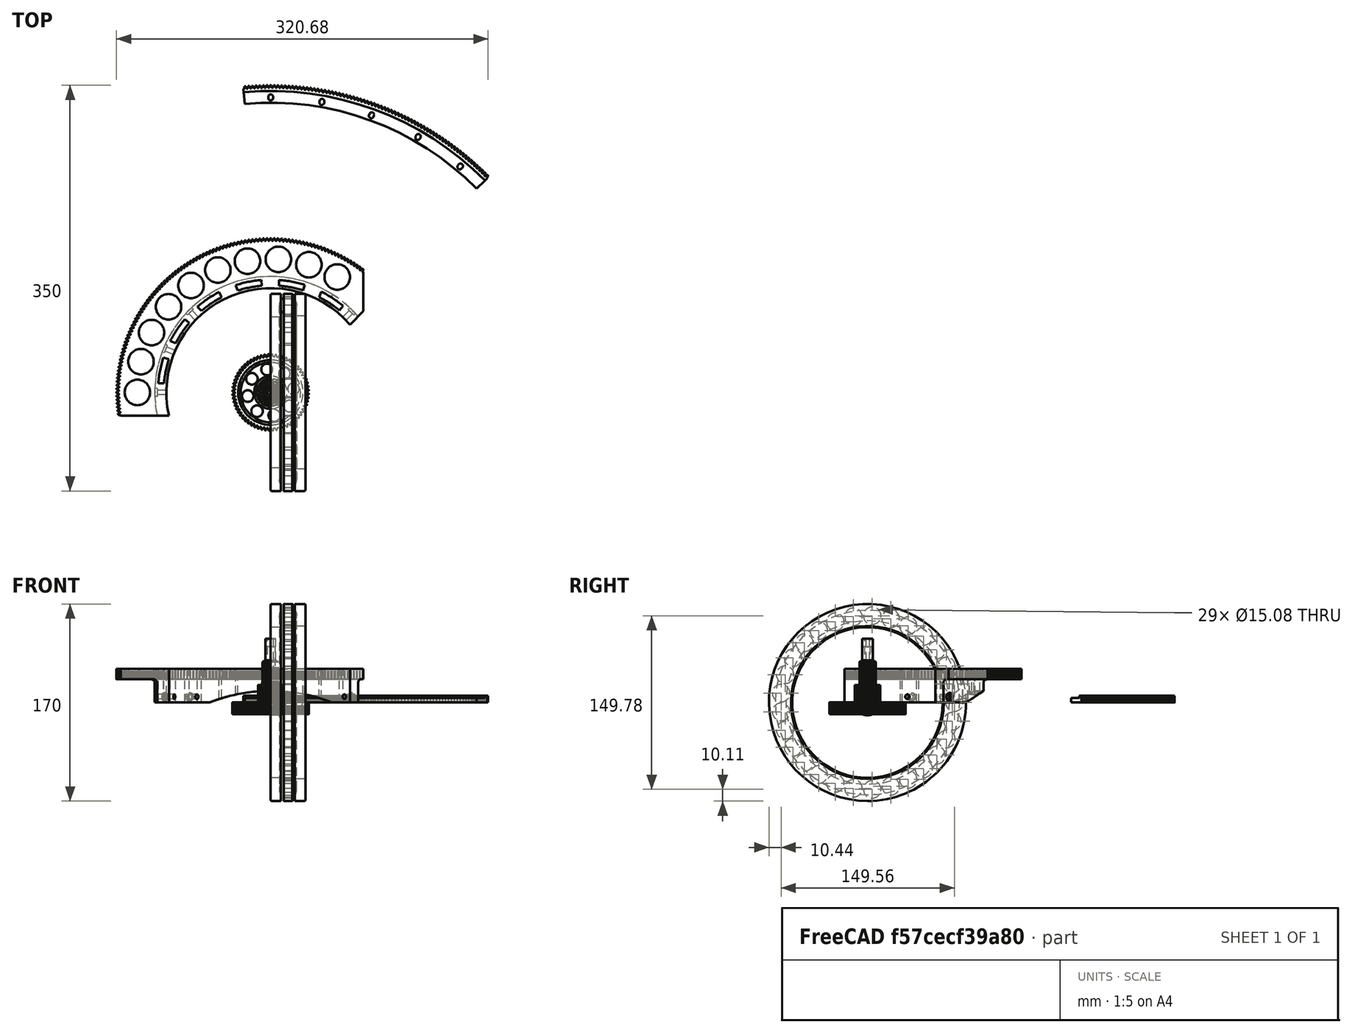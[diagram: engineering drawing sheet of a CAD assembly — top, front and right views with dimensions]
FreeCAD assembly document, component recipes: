
FREECAD ASSEMBLY — COMPONENT RECIPES ("telescope")

This assembly document has 34 components, labeled P0..P33 below (a component is one placed body or linked part). 29 of them carry a construction recipe — the FreeCAD feature program that regenerates the part from scratch, quoted from this document or its linked companion documents; the rest are supplied as boundary geometry only. No exploded tour is included for this assembly.
COMPONENT P0 — recipe-attached ("base-bottom-plate001", modeled in this document).
Construction recipe (the document's own serialized feature program — sketch geometry with constraints, then the solid features built on it; lengths are millimeters unless a unit is written):

FEATURE [Sketcher::SketchObject] Sketch002
  ArcFitTolerance = 0
  AttachmentSupport = -> [XY_Plane]
  ExternalTypes = [0]
  FullyConstrained = true
  MakeInternals = false
  MapMode = 5
  sketch-geometry (1):
    g0: Circle CenterX=0 CenterY=0 CenterZ=0 NormalX=0 NormalY=0 NormalZ=1 AngleXU=0 Radius=7
  constraints (2):
    c: Coincident(g0,g-1)
    c: Diameter(g0) = 14
FEATURE [Sketcher::SketchObject] Sketch
  ArcFitTolerance = 0
  AttachmentSupport = -> [XY_Plane]
  ExternalTypes = [0]
  FullyConstrained = true
  MakeInternals = false
  MapMode = 5
  sketch-geometry (1):
    g0: Circle CenterX=0 CenterY=0 CenterZ=0 NormalX=0 NormalY=0 NormalZ=1 AngleXU=0 Radius=260
  constraints (2):
    c: Coincident(g0,g-1)
    c: Diameter(g0) = 520
FEATURE [PartDesign::Pad] Pad
  AllowMultiFace = false
  Direction = (0,0,1)
  Length = 18
  Length2 = 100
  Profile = -> Sketch
  SideType = 0
  Suppressed = false
  Type = 0
  Type2 = 0
FEATURE [Sketcher::SketchObject] Sketch001
  ArcFitTolerance = 0
  AttachmentSupport = -> [Pad]
  ExternalTypes = [0]
  FullyConstrained = true
  MakeInternals = false
  MapMode = 5
  Placement = pos=(0,0,18) rot=(0,0,1;0rad)
  sketch-geometry (1):
    g0: Circle CenterX=235 CenterY=0 CenterZ=0 NormalX=0 NormalY=0 NormalZ=1 AngleXU=0 Radius=2
  constraints (3):
    c: PointOnObject(g0,g-1)
    c: DistanceX(g0) = 235
    c: Radius(g0) = 2
FEATURE [PartDesign::Pocket] Pocket
  AllowMultiFace = false
  BaseFeature = -> Pad
  Direction = (0,0,-1)
  Length = 5
  Length2 = 100
  Profile = -> Sketch001
  SideType = 0
  Suppressed = false
  Type = 1
  Type2 = 0
FEATURE [PartDesign::PolarPattern] PolarPattern
  Angle = 360
  Axis = -> Sketch001 [N_Axis]
  BaseFeature = -> Pocket
  Mode = 0
  Occurrences = 3
  Offset = 120
  Originals = -> [Pocket]
  SpacingPattern = [0]
  Spacings = [-1,-1]
  Suppressed = false
  TransformMode = 0
FEATURE [PartDesign::Pocket] Pocket001
  BaseFeature = -> PolarPattern
  Direction = (0,0,-1)
  Length = 5
  Length2 = 100
  Profile = -> Sketch002
  Reversed = true
  SideType = 0
  Suppressed = false
  Type = 1
  Type2 = 0
FEATURE [PartDesign::Body] Body  label="base_bottom_plate"
  AllowCompound = true
  Group = -> [Sketch,Pad,Sketch001,Pocket,PolarPattern,Sketch002,Pocket001]
  Origin = -> Origin
  Tip = -> Pocket001
COMPONENT P1 — geometry summary ("bearing-51126_001"; no construction recipe available for this part):
  bounding box: 170.0 x 169.9 x 30.0 mm
  tessellated surface: 256,204 triangles
  volume: 237053 mm^3 (27% of its bounding box)
  symmetry: 2-fold rotationally symmetric about the y axis; revolution-symmetric about the z axis through its bounding-box center; mirror-symmetric across its x mid-plane, z mid-plane
COMPONENT P2 — recipe-attached ("bearing-bottom-location-ring001", modeled in this document).
Construction recipe (the document's own serialized feature program — sketch geometry with constraints, then the solid features built on it; lengths are millimeters unless a unit is written):

FEATURE [Sketcher::SketchObject] Sketch003
  ArcFitTolerance = 0
  AttachmentSupport = -> [XY_Plane003]
  ExternalTypes = [0]
  FullyConstrained = true
  MakeInternals = false
  MapMode = 5
  sketch-geometry (7):
    g0: ArcOfCircle CenterX=0 CenterY=0 CenterZ=0 NormalX=0 NormalY=0 NormalZ=1 AngleXU=0 Radius=60 StartAngle=1.65423 EndAngle=3.58176
    g1: ArcOfCircle CenterX=0 CenterY=0 CenterZ=0 NormalX=0 NormalY=0 NormalZ=1 AngleXU=0 Radius=10 StartAngle=2.0944 EndAngle=3.14159
    g2: LineSegment StartX=-5 StartY=8.66025 StartZ=0 EndX=-5 EndY=59.7913 EndZ=0
    g3: LineSegment [constr] StartX=0 StartY=0 StartZ=0 EndX=-86.6025 EndY=-50 EndZ=0
    g4: LineSegment StartX=-10 StartY=1.2e-15 StartZ=0 EndX=-54.2808 EndY=-25.5655 EndZ=0
    g5: LineSegment [constr] StartX=-10 StartY=1.2e-15 StartZ=0 EndX=0 EndY=0 EndZ=0
    g6: Circle CenterX=0 CenterY=50 CenterZ=0 NormalX=0 NormalY=0 NormalZ=1 AngleXU=0 Radius=2
  constraints (20):
    c: Coincident(g0,g-1)
    c: Coincident(g1,g0)
    c: Vertical(g2)
    c: Coincident(g3,g0)
    c: Angle(g3) = -2.61799
    c: Parallel(g4,g3)
    c: Diameter(g0) = 120
    c: Coincident(g5,g4)
    c: Coincident(g5,g0)
    c: Coincident(g0,g2)
    c: Coincident(g0,g4)
    c: Coincident(g1,g2)
    c: DistanceX(g1) = -5
    c: Diameter(g1) = 20
    c: Distance(g1,g3) = 5
    c: Coincident(g4,g1)
    c: Distance(g3) = 100
    c: PointOnObject(g6,g-2)
    c: Diameter(g6) = 4
    c: DistanceY(g6) = 50
FEATURE [Sketcher::SketchObject] Sketch004
  ArcFitTolerance = 0
  AttachmentSupport = -> [XY_Plane003]
  ExternalTypes = [0]
  FullyConstrained = true
  MakeInternals = false
  MapMode = 5
  sketch-geometry (1):
    g0: Circle CenterX=0 CenterY=0 CenterZ=0 NormalX=0 NormalY=0 NormalZ=1 AngleXU=0 Radius=5.5
  constraints (2):
    c: Coincident(g0,g-1)
    c: Diameter(g0) = 11
FEATURE [Sketcher::SketchObject] Sketch005
  ArcFitTolerance = 0
  AttachmentSupport = -> [XY_Plane003]
  ExternalTypes = [0]
  FullyConstrained = true
  MakeInternals = false
  MapMode = 5
  sketch-geometry (1):
    g0: Circle CenterX=0 CenterY=0 CenterZ=0 NormalX=0 NormalY=0 NormalZ=1 AngleXU=0 Radius=65.25
  constraints (2):
    c: Coincident(g0,g-1)
    c: Diameter(g0) = 130.5
FEATURE [PartDesign::Pad] Pad001
  Direction = (0,0,1)
  Length = 6
  Length2 = 100
  Profile = -> Sketch005
  SideType = 0
  Suppressed = false
  Type = 0
  Type2 = 0
FEATURE [PartDesign::Pocket] Pocket002
  BaseFeature = -> Pad001
  Direction = (0,0,-1)
  Length = 5
  Length2 = 100
  Profile = -> Sketch004
  Reversed = true
  SideType = 0
  Suppressed = false
  Type = 1
  Type2 = 0
FEATURE [PartDesign::Pocket] Pocket003
  BaseFeature = -> Pocket002
  Direction = (0,0,-1)
  Length = 5
  Length2 = 100
  Profile = -> Sketch003
  Reversed = true
  SideType = 0
  Suppressed = false
  Type = 1
  Type2 = 0
FEATURE [PartDesign::PolarPattern] PolarPattern001
  Angle = 360
  Axis = -> Sketch003 [N_Axis]
  BaseFeature = -> Pocket003
  Mode = 0
  Occurrences = 3
  Offset = 120
  Originals = -> [Pocket003]
  SpacingPattern = [0]
  Spacings = [-1,-1]
  Suppressed = false
  TransformMode = 0
FEATURE [PartDesign::Chamfer] Chamfer
  Angle = 45
  Base = -> PolarPattern001 [Edge3,Edge2]
  BaseFeature = -> PolarPattern001
  ChamferType = 0
  FlipDirection = false
  Size = 1
  Size2 = 1
  SupportTransform = true
  Suppressed = false
  UseAllEdges = false
FEATURE [PartDesign::Fillet] Fillet
  Base = -> Chamfer [Edge49,Edge46,Edge54,Edge52,Edge42,Edge40]
  BaseFeature = -> Chamfer
  Radius = 6
  SupportTransform = true
  Suppressed = false
  UseAllEdges = false
FEATURE [Sketcher::SketchObject] Sketch006
  ArcFitTolerance = 0
  AttachmentSupport = -> [Fillet]
  ExternalTypes = [0]
  FullyConstrained = true
  MakeInternals = false
  MapMode = 5
  Placement = pos=(0,0,6) rot=(0,0,1;0rad)
  sketch-geometry (1):
    g0: Circle CenterX=0 CenterY=0 CenterZ=0 NormalX=0 NormalY=0 NormalZ=1 AngleXU=0 Radius=63
  constraints (2):
    c: Coincident(g0,g-1)
    c: Diameter(g0) = 126
FEATURE [PartDesign::Pocket] Pocket004
  BaseFeature = -> Fillet
  Direction = (0,0,-1)
  Length = 3
  Length2 = 100
  Profile = -> Sketch006
  SideType = 0
  Suppressed = false
  Type = 0
  Type2 = 0
FEATURE [PartDesign::Body] Body001  label="bearing-bottom-location-ring"
  AllowCompound = true
  Group = -> [Sketch005,Pad001,Sketch004,Pocket002,Sketch003,Pocket003,PolarPattern001,Chamfer,Fillet,Sketch006,Pocket004]
  Origin = -> Origin003
  Placement = pos=(0,0,18) rot=(0,0,1;0rad)
  Tip = -> Pocket004
COMPONENT P3 — recipe-attached ("m10to14.5-bolt-sleeve001", modeled in this document).
Construction recipe (the document's own serialized feature program — sketch geometry with constraints, then the solid features built on it; lengths are millimeters unless a unit is written):

FEATURE [Sketcher::SketchObject] Sketch007
  ArcFitTolerance = 0
  AttachmentSupport = -> [XY_Plane004]
  ExternalTypes = [0]
  FullyConstrained = true
  MakeInternals = false
  MapMode = 5
  sketch-geometry (2):
    g0: Circle CenterX=0 CenterY=0 CenterZ=0 NormalX=0 NormalY=0 NormalZ=1 AngleXU=0 Radius=5.25
    g1: Circle CenterX=0 CenterY=0 CenterZ=0 NormalX=0 NormalY=0 NormalZ=1 AngleXU=0 Radius=7.25
  constraints (4):
    c: Coincident(g0,g-1)
    c: Coincident(g1,g0)
    c: Diameter(g0) = 10.5
    c: Diameter(g1) = 14.5
FEATURE [PartDesign::Pad] Pad002
  Direction = (0,0,1)
  Length = 17
  Length2 = 100
  Profile = -> Sketch007
  SideType = 0
  Suppressed = false
  Type = 0
  Type2 = 0
FEATURE [PartDesign::Chamfer] Chamfer001
  Angle = 45
  Base = -> Pad002 [Edge3]
  BaseFeature = -> Pad002
  ChamferType = 0
  FlipDirection = false
  Size = 1
  Size2 = 1
  SupportTransform = true
  Suppressed = false
  UseAllEdges = false
FEATURE [PartDesign::Body] Body002  label="m10to14.5-bolt-sleeve"
  AllowCompound = true
  Group = -> [Sketch007,Pad002,Chamfer001]
  Origin = -> Origin004
  Tip = -> Chamfer001
COMPONENT P4 — recipe-attached ("fork-bottom-plate001", modeled in this document).
Construction recipe (the document's own serialized feature program — sketch geometry with constraints, then the solid features built on it; lengths are millimeters unless a unit is written):

FEATURE [Sketcher::SketchObject] Sketch012
  ArcFitTolerance = 0
  AttachmentSupport = -> [XY_Plane009]
  ExternalTypes = [0]
  FullyConstrained = true
  MakeInternals = false
  MapMode = 5
  sketch-geometry (1):
    g0: Circle CenterX=0 CenterY=0 CenterZ=0 NormalX=0 NormalY=0 NormalZ=1 AngleXU=0 Radius=7
  constraints (2):
    c: Coincident(g0,g-1)
    c: Diameter(g0) = 14
FEATURE [Sketcher::SketchObject] Sketch013
  ArcFitTolerance = 0
  AttachmentSupport = -> [XY_Plane009]
  ExternalTypes = [0]
  FullyConstrained = true
  MakeInternals = false
  MapMode = 5
  sketch-geometry (1):
    g0: Circle CenterX=0 CenterY=0 CenterZ=0 NormalX=0 NormalY=0 NormalZ=1 AngleXU=0 Radius=260
  constraints (2):
    c: Coincident(g0,g-1)
    c: Radius(g0) = 260
FEATURE [PartDesign::Pad] Pad003
  AllowMultiFace = false
  Direction = (0,0,1)
  Length = 18
  Length2 = 100
  Profile = -> Sketch013
  SideType = 0
  Suppressed = false
  Type = 0
  Type2 = 0
FEATURE [PartDesign::Pocket] Pocket009
  BaseFeature = -> Pad003
  Direction = (0,0,-1)
  Length = 5
  Length2 = 100
  Profile = -> Sketch012
  Reversed = true
  SideType = 0
  Suppressed = false
  Type = 1
  Type2 = 0
FEATURE [Sketcher::SketchObject] Sketch014
  ArcFitTolerance = 0
  AttachmentSupport = -> [Pocket009]
  ExternalTypes = [0]
  FullyConstrained = true
  MakeInternals = false
  MapMode = 5
  Placement = pos=(0,0,18) rot=(0,0,1;0rad)
  sketch-geometry (4):
    g0: LineSegment StartX=-170 StartY=150 StartZ=0 EndX=170 EndY=150 EndZ=0
    g1: LineSegment StartX=-170 StartY=150 StartZ=0 EndX=-170 EndY=0 EndZ=0
    g2: LineSegment StartX=170 StartY=150 StartZ=0 EndX=170 EndY=0 EndZ=0
    g3: LineSegment StartX=-28 StartY=-227 StartZ=0 EndX=28 EndY=-227 EndZ=0
  constraints (12):
    c: Symmetric(g0,g0,g-2)
    c: DistanceX(g0,g0) = 340
    c: DistanceY(g0) = 150
    c: Coincident(g1,g0)
    c: PointOnObject(g1,g-1)
    c: Vertical(g1)
    c: Coincident(g2,g0)
    c: PointOnObject(g2,g-1)
    c: Vertical(g2)
    c: Symmetric(g3,g3,g-2)
    c: DistanceX(g3,g3) = 56
    c: DistanceY(g3) = -227
FEATURE [PartDesign::Body] Body004  label="fork-bottom-plate"
  AllowCompound = true
  Group = -> [Sketch013,Pad003,Sketch012,Pocket009,Sketch014]
  Origin = -> Origin009
  Placement = pos=(0,0,48) rot=(0,0,1;0.004518rad)
  Tip = -> Pocket009
COMPONENT P5 — recipe-attached ("vertical-axis-main-gear001", modeled in this document).
Construction recipe (the document's own serialized feature program — sketch geometry with constraints, then the solid features built on it; lengths are millimeters unless a unit is written):

FEATURE [PartDesign::FeatureBase] BaseFeature
  BaseFeature = -> InvoluteGear004
  Suppressed = false
FEATURE [Sketcher::SketchObject] Sketch008
  ArcFitTolerance = 0
  AttachmentSupport = -> [BaseFeature]
  ExternalTypes = [0]
  FullyConstrained = true
  MakeInternals = false
  MapMode = 5
  Placement = pos=(0,0,6) rot=(0,0,1;0rad)
  sketch-geometry (1):
    g0: Circle CenterX=0 CenterY=0 CenterZ=0 NormalX=0 NormalY=0 NormalZ=1 AngleXU=0 Radius=260
  constraints (2):
    c: Coincident(g0,g-1)
    c: Diameter(g0) = 520
FEATURE [PartDesign::Pocket] Pocket005
  BaseFeature = -> BaseFeature
  Direction = (0,0,-1)
  Length = 2
  Length2 = 100
  Profile = -> Sketch008
  SideType = 0
  Suppressed = false
  Type = 0
  Type2 = 0
FEATURE [Sketcher::SketchObject] Sketch009
  ArcFitTolerance = 0
  AttachmentSupport = -> [Pocket005]
  ExternalTypes = [0]
  FullyConstrained = true
  MakeInternals = false
  MapMode = 5
  Placement = pos=(0,0,4) rot=(0,0,1;0rad)
  sketch-geometry (1):
    g0: Circle CenterX=0 CenterY=0 CenterZ=0 NormalX=0 NormalY=0 NormalZ=1 AngleXU=0 Radius=250
  constraints (2):
    c: Coincident(g0,g-1)
    c: Diameter(g0) = 500
FEATURE [PartDesign::Pocket] Pocket006
  BaseFeature = -> Pocket005
  Direction = (0,0,-1)
  Length = 5
  Length2 = 100
  Profile = -> Sketch009
  SideType = 0
  Suppressed = false
  Type = 1
  Type2 = 0
FEATURE [Sketcher::SketchObject] Sketch010
  ArcFitTolerance = 0
  AttachmentSupport = -> [Pocket006]
  ExternalTypes = [0]
  FullyConstrained = true
  MakeInternals = false
  MapMode = 5
  Placement = pos=(0,0,4) rot=(0,0,1;0rad)
  sketch-geometry (4):
    g0: ArcOfCircle CenterX=0 CenterY=254 CenterZ=0 NormalX=0 NormalY=0 NormalZ=1 AngleXU=0 Radius=2.1 StartAngle=3.14159 EndAngle=6.28319
    g1: ArcOfCircle CenterX=2e-16 CenterY=255 CenterZ=0 NormalX=0 NormalY=0 NormalZ=1 AngleXU=0 Radius=2.1 StartAngle=4.6e-15 EndAngle=3.14159
    g2: LineSegment StartX=2.1 StartY=254 StartZ=0 EndX=2.1 EndY=255 EndZ=0
    g3: LineSegment StartX=-2.1 StartY=254 StartZ=0 EndX=-2.1 EndY=255 EndZ=0
  constraints (10):
    c: Tangent(g0,g3) = 1.5708
    c: Tangent(g0,g2) = -1.5708
    c: Tangent(g2,g1) = -1.5708
    c: Tangent(g3,g1) = 1.5708
    c: Vertical(g2)
    c: Equal(g0,g1)
    c: PointOnObject(g0,g-2)
    c: Diameter(g0) = 4.2
    c: DistanceY(g2,g2) = 1
    c: DistanceY(g0) = 254
FEATURE [PartDesign::Pocket] Pocket007
  BaseFeature = -> Pocket006
  Direction = (0,0,-1)
  Length = 5
  Length2 = 100
  Profile = -> Sketch010
  SideType = 0
  Suppressed = false
  Type = 1
  Type2 = 0
FEATURE [PartDesign::PolarPattern] PolarPattern002
  Angle = 360
  Axis = -> Sketch010 [N_Axis]
  BaseFeature = -> Pocket007
  Mode = 0
  Occurrences = 36
  Offset = 120
  Originals = -> [Pocket007]
  SpacingPattern = [0]
  Spacings = [-1,-1,-1,-1,-1,-1,-1,-1,-1,-1,-1,-1,-1,-1,-1,-1,-1,-1,-1,-1,-1,-1,-1,-1,-1,-1,-1,-1,-1,-1,-1,-1,-1,-1,-1]
  Suppressed = false
  TransformMode = 0
FEATURE [Sketcher::SketchObject] Sketch011
  ArcFitTolerance = 0
  AttachmentSupport = -> [PolarPattern002]
  ExternalTypes = [0]
  FullyConstrained = true
  MakeInternals = false
  MapMode = 5
  Placement = pos=(0,0,6) rot=(0,0,1;0rad)
  sketch-geometry (3):
    g0: LineSegment StartX=-26.7392 StartY=298.806 StartZ=0 EndX=3.6e-15 EndY=0 EndZ=0
    g1: LineSegment StartX=0 StartY=0 StartZ=0 EndX=213.39 EndY=210.866 EndZ=0
    g2: ArcOfCircle CenterX=0 CenterY=0 CenterZ=0 NormalX=0 NormalY=0 NormalZ=1 AngleXU=0 Radius=300 StartAngle=1.66005 EndAngle=7.06263
  constraints (8):
    c: Coincident(g0,g-1)
    c: Coincident(g1,g0)
    c: Angle(g-2,g0) = 0.0892492
    c: Coincident(g2,g0)
    c: Coincident(g2,g0)
    c: Coincident(g2,g1)
    c: Distance(g0) = 300
    c: Angle(g1,g0) = 0.880597
FEATURE [PartDesign::Pocket] Pocket008
  BaseFeature = -> PolarPattern002
  Direction = (0,0,-1)
  Length = 5
  Length2 = 100
  Profile = -> Sketch011
  SideType = 0
  Suppressed = false
  Type = 1
  Type2 = 0
FEATURE [PartDesign::Body] Body003  label="gear_ring"
  AllowCompound = true
  BaseFeature = -> InvoluteGear004
  Group = -> [BaseFeature,Sketch008,Pocket005,Sketch009,Pocket006,Sketch010,Pocket007,PolarPattern002,Sketch011,Pocket008]
  Origin = -> Origin005
  Tip = -> Pocket008
COMPONENT P6 — same part as P5; its construction recipe is shown at P5.
COMPONENT P7 — same part as P5; its construction recipe is shown at P5.
COMPONENT P8 — same part as P3; its construction recipe is shown at P3.
COMPONENT P9 — recipe-attached ("vertical-axis-motor-mount001", modeled in this document).
Construction recipe (the document's own serialized feature program — sketch geometry with constraints, then the solid features built on it; lengths are millimeters unless a unit is written):

FEATURE [Sketcher::SketchObject] Sketch021
  ArcFitTolerance = 0
  AttachmentSupport = -> [XY_Plane012]
  ExternalTypes = [0]
  FullyConstrained = true
  MakeInternals = false
  MapMode = 5
  sketch-geometry (4):
    g0: ArcOfCircle CenterX=-28 CenterY=15 CenterZ=0 NormalX=0 NormalY=0 NormalZ=1 AngleXU=0 Radius=2 StartAngle=3.14159 EndAngle=6.28319
    g1: ArcOfCircle CenterX=-28 CenterY=25 CenterZ=0 NormalX=0 NormalY=0 NormalZ=1 AngleXU=0 Radius=2 StartAngle=0 EndAngle=3.14159
    g2: LineSegment StartX=-26 StartY=15 StartZ=0 EndX=-26 EndY=25 EndZ=0
    g3: LineSegment StartX=-30 StartY=15 StartZ=0 EndX=-30 EndY=25 EndZ=0
  constraints (10):
    c: Tangent(g0,g3) = 1.5708
    c: Tangent(g0,g2) = -1.5708
    c: Tangent(g2,g1) = -1.5708
    c: Tangent(g3,g1) = 1.5708
    c: Vertical(g2)
    c: Equal(g0,g1)
    c: Radius(g1) = 2
    c: DistanceY(g0,g1) = 10
    c: DistanceY(g0) = 15
    c: DistanceX(g0,g-1) = 28
FEATURE [PartDesign::LinearPattern] LinearPattern
  Direction = -> Sketch021 [H_Axis]
  Length = 56
  Length2 = 100
  Mode = 0
  Mode2 = 0
  Occurrences = 2
  Occurrences2 = 1
  Offset = 56
  Offset2 = 10
  Reversed2 = false
  SpacingPattern = [0]
  SpacingPattern2 = [0]
  Spacings = [-1]
  Suppressed = false
  TransformMode = 0
FEATURE [PartDesign::LinearPattern] LinearPattern001
  Direction = -> Sketch021 [V_Axis]
  Length = 18
  Length2 = 100
  Mode = 0
  Mode2 = 0
  Occurrences = 2
  Occurrences2 = 1
  Offset = 18
  Offset2 = 10
  Reversed2 = false
  SpacingPattern = [0]
  SpacingPattern2 = [0]
  Spacings = [-1]
  Suppressed = false
  TransformMode = 0
FEATURE [Sketcher::SketchObject] Sketch022
  ArcFitTolerance = 0
  ExternalTypes = [0]
  FullyConstrained = true
  MakeInternals = false
  MapMode = 5
  Placement = pos=(0,0,5) rot=(0,0,1;0rad)
  sketch-geometry (4):
    g0: Circle CenterX=-15.5 CenterY=15.5 CenterZ=0 NormalX=0 NormalY=0 NormalZ=1 AngleXU=0 Radius=2
    g1: Circle CenterX=15.5 CenterY=15.5 CenterZ=0 NormalX=0 NormalY=0 NormalZ=1 AngleXU=0 Radius=2
    g2: Circle CenterX=15.5 CenterY=-15.5 CenterZ=0 NormalX=0 NormalY=0 NormalZ=1 AngleXU=0 Radius=2
    g3: Circle CenterX=-15.5 CenterY=-15.5 CenterZ=0 NormalX=0 NormalY=0 NormalZ=1 AngleXU=0 Radius=2
  constraints (9):
    c: Symmetric(g3,g0,g-1)
    c: Symmetric(g0,g1,g-2)
    c: Symmetric(g2,g1,g-1)
    c: Equal(g3,g2)
    c: Equal(g2,g1)
    c: Equal(g1,g0)
    c: DistanceX(g0,g1) = 31
    c: DistanceY(g2,g1) = 31
    c: Diameter(g1) = 4
FEATURE [Sketcher::SketchObject] Sketch023
  ArcFitTolerance = 0
  AttachmentSupport = -> [XY_Plane012]
  ExternalTypes = [0]
  FullyConstrained = true
  MakeInternals = false
  MapMode = 5
  sketch-geometry (5):
    g0: LineSegment StartX=25 StartY=25 StartZ=0 EndX=-25 EndY=25 EndZ=0
    g1: LineSegment StartX=-25 StartY=-25 StartZ=0 EndX=25 EndY=-25 EndZ=0
    g2: Circle [constr] CenterX=0 CenterY=0 CenterZ=0 NormalX=0 NormalY=0 NormalZ=1 AngleXU=0 Radius=35.3553
    g3: LineSegment StartX=-25 StartY=25 StartZ=0 EndX=-25 EndY=-25 EndZ=0
    g4: LineSegment StartX=25 StartY=25 StartZ=0 EndX=25 EndY=-25 EndZ=0
  constraints (14):
    c: Equal(g0,g1)
    c: PointOnObject(g0,g2)
    c: PointOnObject(g1,g2)
    c: PointOnObject(g1,g2)
    c: PointOnObject(g0,g2)
    c: Coincident(g2,g-1)
    c: Horizontal(g0)
    c: DistanceX(g0,g0) = 50
    c: DistanceY(g1,g0) = 50
    c: Horizontal(g1)
    c: Coincident(g0,g3)
    c: Coincident(g3,g1)
    c: Coincident(g0,g4)
    c: Coincident(g4,g1)
FEATURE [PartDesign::Pad] Pad005
  Direction = (0,0,1)
  Length = 10
  Length2 = 100
  Profile = -> Sketch023
  Refine = true
  SideType = 0
  Suppressed = false
  Type = 0
  Type2 = 0
FEATURE [Sketcher::SketchObject] Sketch024
  ArcFitTolerance = 0
  AttachmentSupport = -> [Pad005]
  ExternalTypes = [0]
  FullyConstrained = true
  MakeInternals = false
  MapMode = 5
  Placement = pos=(0,0,10) rot=(0,0,1;0rad)
  sketch-geometry (5):
    g0: LineSegment StartX=21 StartY=21 StartZ=0 EndX=-21 EndY=21 EndZ=0
    g1: LineSegment StartX=-21 StartY=21 StartZ=0 EndX=-21 EndY=-21 EndZ=0
    g2: LineSegment StartX=-21 StartY=-21 StartZ=0 EndX=21 EndY=-21 EndZ=0
    g3: LineSegment StartX=21 StartY=-21 StartZ=0 EndX=21 EndY=21 EndZ=0
    g4: Circle [constr] CenterX=0 CenterY=0 CenterZ=0 NormalX=0 NormalY=0 NormalZ=1 AngleXU=0 Radius=29.6985
  constraints (14):
    c: Coincident(g0,g1)
    c: Coincident(g1,g2)
    c: Coincident(g2,g3)
    c: Coincident(g3,g0)
    c: Equal(g0,g1)
    c: Equal(g0,g2)
    c: Equal(g0,g3)
    c: PointOnObject(g0,g4)
    c: PointOnObject(g1,g4)
    c: PointOnObject(g2,g4)
    c: PointOnObject(g3,g4)
    c: Coincident(g4,g-1)
    c: DistanceX(g0,g0) = 42
    c: Horizontal(g0)
FEATURE [PartDesign::Pocket] Pocket014
  BaseFeature = -> Pad005
  Direction = (0,0,-1)
  Length = 7
  Length2 = 100
  Profile = -> Sketch024
  Refine = true
  SideType = 0
  Suppressed = false
  Type = 0
  Type2 = 0
FEATURE [Sketcher::SketchObject] Sketch025
  ArcFitTolerance = 0
  AttachmentSupport = -> [Pocket014]
  ExternalTypes = [0]
  FullyConstrained = true
  MakeInternals = false
  MapMode = 5
  Placement = pos=(0,0,3) rot=(0,0,1;0rad)
  sketch-geometry (1):
    g0: Circle CenterX=0 CenterY=0 CenterZ=0 NormalX=0 NormalY=0 NormalZ=1 AngleXU=0 Radius=11
  constraints (2):
    c: Coincident(g0,g-1)
    c: Diameter(g0) = 22
FEATURE [PartDesign::Pocket] Pocket015
  BaseFeature = -> Pocket014
  Direction = (0,0,-1)
  Length = 5
  Length2 = 100
  Profile = -> Sketch025
  Refine = true
  SideType = 0
  Suppressed = false
  Type = 1
  Type2 = 0
FEATURE [PartDesign::Pocket] Pocket016
  BaseFeature = -> Pocket015
  Direction = (0,0,-1)
  Length = 5
  Length2 = 100
  Profile = -> Sketch022
  Refine = true
  SideType = 0
  Suppressed = false
  Type = 0
  Type2 = 0
FEATURE [Sketcher::SketchObject] Sketch026
  ArcFitTolerance = 0
  AttachmentSupport = -> [XY_Plane012]
  ExternalGeometry = -> [Pocket016]
  ExternalTypes = [0]
  FullyConstrained = true
  MakeInternals = false
  MapMode = 5
  sketch-geometry (8):
    g0: LineSegment StartX=-25 StartY=25 StartZ=0 EndX=25 EndY=25 EndZ=0
    g1: LineSegment StartX=35 StartY=-7.67949 StartZ=0 EndX=35 EndY=50 EndZ=0
    g2: LineSegment StartX=35 StartY=50 StartZ=0 EndX=-35 EndY=50 EndZ=0
    g3: LineSegment StartX=-35 StartY=50 StartZ=0 EndX=-35 EndY=-7.67949 EndZ=0
    g4: LineSegment StartX=-35 StartY=-7.67949 StartZ=0 EndX=-25 EndY=-25 EndZ=0
    g5: LineSegment StartX=-25 StartY=-25 StartZ=0 EndX=-25 EndY=25 EndZ=0
    g6: LineSegment StartX=35 StartY=-7.67949 StartZ=0 EndX=25 EndY=-25 EndZ=0
    g7: LineSegment StartX=25 StartY=-25 StartZ=0 EndX=25 EndY=25 EndZ=0
  constraints (19):
    c: Coincident(g-3,g0)
    c: Coincident(g0,g-3)
    c: Vertical(g1)
    c: Coincident(g1,g2)
    c: Coincident(g2,g3)
    c: Symmetric(g2,g1,g-2)
    c: Symmetric(g3,g1,g-2)
    c: DistanceX(g2,g2) = 70
    c: DistanceY(g1) = 50
    c: Coincident(g3,g4)
    c: Coincident(g4,g5)
    c: Coincident(g5,g0)
    c: Vertical(g5)
    c: Coincident(g1,g6)
    c: Coincident(g6,g7)
    c: Coincident(g7,g0)
    c: Symmetric(g6,g4,g-2)
    c: Angle(g1,g6) = 2.61799
    c: DistanceY(g6) = -25
FEATURE [PartDesign::Pad] Pad006
  BaseFeature = -> Pocket016
  Direction = (0,0,1)
  Length = 10
  Length2 = 100
  Profile = -> Sketch026
  Refine = true
  SideType = 0
  Suppressed = false
  Type = 0
  Type2 = 0
FEATURE [PartDesign::Pocket] Pocket017
  BaseFeature = -> Pad006
  Direction = (0,0,-1)
  Length = 5
  Length2 = 100
  Profile = -> Sketch021
  Refine = true
  Reversed = true
  SideType = 0
  Suppressed = false
  Type = 1
  Type2 = 0
FEATURE [PartDesign::MultiTransform] MultiTransform
  BaseFeature = -> Pocket017
  Originals = -> [Pocket017]
  Refine = true
  Suppressed = false
  TransformMode = 0
  Transformations = -> [LinearPattern,LinearPattern001]
FEATURE [PartDesign::Fillet] Fillet002
  Base = -> MultiTransform [Edge5,Edge1,Edge2,Edge58,Edge59,Edge8]
  BaseFeature = -> MultiTransform
  Radius = 5
  SupportTransform = true
  Suppressed = false
  UseAllEdges = false
FEATURE [PartDesign::Body] Body007  label="vertical-axis-motor-mount"
  AllowCompound = true
  Group = -> [Sketch023,Pad005,Sketch024,Pocket014,Sketch025,Pocket015,Sketch022,Pocket016,Sketch026,Pad006,Sketch021,Pocket017,MultiTransform,LinearPattern,LinearPattern001,Fillet002]
  Origin = -> Origin012
  Placement = pos=(0,0,232.808) rot=(0,0,1;0rad)
  Tip = -> Fillet002
COMPONENT P10 — recipe-attached ("nema17_001", modeled in this document).
Construction recipe (the document's own serialized feature program — sketch geometry with constraints, then the solid features built on it; lengths are millimeters unless a unit is written):

FEATURE [Sketcher::SketchObject] Sketch027
  ArcFitTolerance = 0
  AttachmentSupport = -> [XY_Plane013]
  ExternalTypes = [0]
  FullyConstrained = true
  MakeInternals = false
  MapMode = 5
  sketch-geometry (5):
    g0: LineSegment StartX=21.15 StartY=21.15 StartZ=0 EndX=-21.15 EndY=21.15 EndZ=0
    g1: LineSegment StartX=-21.15 StartY=21.15 StartZ=0 EndX=-21.15 EndY=-21.15 EndZ=0
    g2: LineSegment StartX=-21.15 StartY=-21.15 StartZ=0 EndX=21.15 EndY=-21.15 EndZ=0
    g3: LineSegment StartX=21.15 StartY=-21.15 StartZ=0 EndX=21.15 EndY=21.15 EndZ=0
    g4: Circle [constr] CenterX=0 CenterY=0 CenterZ=0 NormalX=0 NormalY=0 NormalZ=1 AngleXU=0 Radius=29.9106
  constraints (14):
    c: Coincident(g0,g1)
    c: Coincident(g1,g2)
    c: Coincident(g2,g3)
    c: Coincident(g3,g0)
    c: Equal(g0,g1)
    c: Equal(g0,g2)
    c: Equal(g0,g3)
    c: PointOnObject(g0,g4)
    c: PointOnObject(g1,g4)
    c: PointOnObject(g2,g4)
    c: PointOnObject(g3,g4)
    c: Coincident(g4,g-1)
    c: Horizontal(g0)
    c: DistanceY(g3,g3) = 42.3
FEATURE [PartDesign::Pad] Pad007
  Direction = (0,0,1)
  Length = 40
  Length2 = 100
  Profile = -> Sketch027
  SideType = 0
  Suppressed = false
  Type = 0
  Type2 = 0
FEATURE [Sketcher::SketchObject] Sketch028
  ArcFitTolerance = 0
  AttachmentSupport = -> [Pad007]
  ExternalTypes = [0]
  FullyConstrained = true
  MakeInternals = false
  MapMode = 5
  Placement = pos=(0,0,40) rot=(0,0,1;0rad)
  sketch-geometry (1):
    g0: Circle CenterX=0 CenterY=0 CenterZ=0 NormalX=0 NormalY=0 NormalZ=1 AngleXU=0 Radius=11
  constraints (2):
    c: Coincident(g0,g-1)
    c: Diameter(g0) = 22
FEATURE [PartDesign::Pad] Pad008
  BaseFeature = -> Pad007
  Direction = (0,0,1)
  Length = 2
  Length2 = 100
  Profile = -> Sketch028
  SideType = 0
  Suppressed = false
  Type = 0
  Type2 = 0
FEATURE [Sketcher::SketchObject] Sketch029
  ArcFitTolerance = 0
  AttachmentSupport = -> [Pad008]
  ExternalTypes = [0]
  FullyConstrained = true
  MakeInternals = false
  MapMode = 5
  Placement = pos=(0,0,40) rot=(0,0,1;0rad)
  sketch-geometry (1):
    g0: Circle CenterX=0 CenterY=0 CenterZ=0 NormalX=0 NormalY=0 NormalZ=1 AngleXU=0 Radius=2.5
  constraints (2):
    c: Coincident(g0,g-1)
    c: Diameter(g0) = 5
FEATURE [PartDesign::Pad] Pad009
  BaseFeature = -> Pad008
  Direction = (0,0,1)
  Length = 24
  Length2 = 100
  Profile = -> Sketch029
  SideType = 0
  Suppressed = false
  Type = 0
  Type2 = 0
FEATURE [PartDesign::Chamfer] Chamfer004
  Angle = 45
  Base = -> Pad009 [Edge18]
  BaseFeature = -> Pad009
  ChamferType = 0
  FlipDirection = false
  Size = 0.5
  Size2 = 1
  SupportTransform = true
  Suppressed = false
  UseAllEdges = false
FEATURE [Sketcher::SketchObject] Sketch030
  ArcFitTolerance = 0
  AttachmentSupport = -> [XZ_Plane013]
  ExternalGeometry = -> [Chamfer004]
  ExternalTypes = [0]
  FullyConstrained = true
  MakeInternals = false
  MapMode = 5
  Placement = pos=(0,0,0) rot=(1,0,0;1.5708rad)
  sketch-geometry (4):
    g0: LineSegment StartX=2 StartY=64 StartZ=0 EndX=2.5 EndY=64 EndZ=0
    g1: LineSegment StartX=2.5 StartY=64 StartZ=0 EndX=2.5 EndY=43 EndZ=0
    g2: LineSegment StartX=2.5 StartY=43 StartZ=0 EndX=2 EndY=43 EndZ=0
    g3: LineSegment StartX=2 StartY=43 StartZ=0 EndX=2 EndY=64 EndZ=0
  constraints (12):
    c: Coincident(g0,g1)
    c: Coincident(g1,g2)
    c: Coincident(g2,g3)
    c: Coincident(g3,g0)
    c: Horizontal(g0)
    c: Horizontal(g2)
    c: Vertical(g1)
    c: Vertical(g3)
    c: PointOnObject(g0,g-3)
    c: PointOnObject(g1,g-4)
    c: DistanceX(g2,g2) = 0.5
    c: DistanceY(g1,g1) = 21
FEATURE [PartDesign::Pocket] Pocket018
  BaseFeature = -> Chamfer004
  Direction = (0,1,-2e-16)
  Length = 20
  Length2 = 100
  Profile = -> Sketch030
  SideType = 2
  Suppressed = false
  Type = 1
  Type2 = 0
FEATURE [Sketcher::SketchObject] Sketch031
  ArcFitTolerance = 0
  AttachmentSupport = -> [Pocket018]
  ExternalTypes = [0]
  FullyConstrained = true
  MakeInternals = false
  MapMode = 5
  Placement = pos=(0,0,40) rot=(0,0,1;0rad)
  sketch-geometry (4):
    g0: Circle CenterX=15.5 CenterY=-15.5 CenterZ=0 NormalX=0 NormalY=0 NormalZ=1 AngleXU=0 Radius=1.25
    g1: Circle CenterX=15.5 CenterY=15.5 CenterZ=0 NormalX=0 NormalY=0 NormalZ=1 AngleXU=0 Radius=1.25
    g2: Circle CenterX=-15.5 CenterY=15.5 CenterZ=0 NormalX=0 NormalY=0 NormalZ=1 AngleXU=0 Radius=1.25
    g3: Circle CenterX=-15.5 CenterY=-15.5 CenterZ=0 NormalX=0 NormalY=0 NormalZ=1 AngleXU=0 Radius=1.25
  constraints (9):
    c: Diameter(g0) = 2.5
    c: Symmetric(g1,g0,g-1)
    c: Symmetric(g1,g2,g-2)
    c: Symmetric(g3,g2,g-1)
    c: Equal(g2,g1)
    c: Equal(g1,g3)
    c: Equal(g3,g0)
    c: DistanceX(g2,g1) = 31
    c: DistanceY(g0,g1) = 31
FEATURE [PartDesign::Hole] Hole
  BaseFeature = -> Pocket018
  BaseProfileType = 6
  CustomThreadClearance = 0
  Depth = 4
  DepthType = 0
  Diameter = 1.4
  DrillForDepth = false
  DrillPoint = 1
  DrillPointAngle = 118
  HoleCutCountersinkAngle = 90
  HoleCutCustomValues = false
  HoleCutDepth = 0
  HoleCutDiameter = 1.6
  HoleCutType = 0
  ModelThread = false
  Profile = -> Sketch031
  Suppressed = false
  Tapered = false
  TaperedAngle = 90
  ThreadClass = 0
  ThreadDepth = 4
  ThreadDepthType = 0
  ThreadDiameter = 1.2
  ThreadDirection = 0
  ThreadFit = 0
  ThreadSize = 2
  ThreadType = 1
  Threaded = false
  UseCustomThreadClearance = false
FEATURE [PartDesign::Chamfer] Chamfer005
  Angle = 45
  Base = -> Hole [Edge29,Edge26,Edge31,Edge27]
  BaseFeature = -> Hole
  ChamferType = 0
  FlipDirection = false
  Size = 5
  Size2 = 1
  SupportTransform = true
  Suppressed = false
  UseAllEdges = false
FEATURE [PartDesign::Body] Body008  label="nema17"
  AllowCompound = true
  Group = -> [Sketch027,Pad007,Sketch028,Pad008,Sketch029,Pad009,Chamfer004,Sketch030,Pocket018,Sketch031,Hole,Chamfer005]
  Origin = -> Origin013
  Tip = -> Chamfer005
COMPONENT P11 — recipe-attached ("vertical-axis-motor-gear001", modeled in this document).
Construction recipe (the document's own serialized feature program — sketch geometry with constraints, then the solid features built on it; lengths are millimeters unless a unit is written):

FEATURE [PartDesign::FeatureBase] BaseFeature001
  BaseFeature = -> InvoluteGear005
  Suppressed = false
FEATURE [Sketcher::SketchObject] Sketch032
  ArcFitTolerance = 0
  AttachmentSupport = -> [BaseFeature001]
  ExternalTypes = [0]
  FullyConstrained = true
  MakeInternals = false
  MapMode = 5
  Placement = pos=(0,0,55) rot=(0,0,1;0rad)
  sketch-geometry (2):
    g0: ArcOfCircle CenterX=0 CenterY=0 CenterZ=0 NormalX=0 NormalY=0 NormalZ=1 AngleXU=0 Radius=2.5 StartAngle=0.643501 EndAngle=5.63968
    g1: LineSegment StartX=2 StartY=1.5 StartZ=0 EndX=2 EndY=-1.5 EndZ=0
  constraints (6):
    c: Coincident(g0,g-1)
    c: Diameter(g0) = 5
    c: Vertical(g1)
    c: Coincident(g0,g1)
    c: Coincident(g0,g1)
    c: DistanceX(g0) = 2
FEATURE [PartDesign::Pocket] Pocket019
  BaseFeature = -> BaseFeature001
  Direction = (0,0,-1)
  Length = 25
  Length2 = 100
  Profile = -> Sketch032
  SideType = 0
  Suppressed = false
  Type = 0
  Type2 = 0
FEATURE [Sketcher::SketchObject] Sketch033
  ArcFitTolerance = 0
  AttachmentSupport = -> [XZ_Plane014]
  ExternalGeometry = -> [Pocket019]
  ExternalTypes = [0]
  FullyConstrained = true
  MakeInternals = false
  MapMode = 5
  Placement = pos=(0,0,0) rot=(1,0,0;1.5708rad)
  sketch-geometry (4):
    g0: LineSegment StartX=4.5 StartY=36.4434 StartZ=0 EndX=4.5 EndY=55 EndZ=0
    g1: LineSegment StartX=4.5 StartY=55 StartZ=0 EndX=7 EndY=55 EndZ=0
    g2: LineSegment StartX=7 StartY=55 StartZ=0 EndX=7 EndY=35 EndZ=0
    g3: LineSegment StartX=7 StartY=35 StartZ=0 EndX=4.5 EndY=36.4434 EndZ=0
  constraints (12):
    c: Vertical(g0)
    c: Coincident(g0,g1)
    c: Coincident(g1,g2)
    c: Vertical(g2)
    c: Coincident(g2,g3)
    c: Coincident(g3,g0)
    c: DistanceX(g0) = 4.5
    c: DistanceX(g2) = 7
    c: DistanceY(g2,g2) = 20
    c: Horizontal(g1)
    c: Horizontal(g1,g-3)
    c: Angle(g2,g3) = 1.0472
FEATURE [PartDesign::Groove] Groove
  Angle = 360
  Angle2 = 60
  Axis = (0,2e-16,1)
  Base = (0,0,0)
  BaseFeature = -> Pocket019
  Profile = -> Sketch033
  ReferenceAxis = -> Sketch033 [V_Axis]
  Suppressed = false
  Type = 0
FEATURE [PartDesign::Body] Body009  label="vertical-axis-gear"
  AllowCompound = true
  BaseFeature = -> InvoluteGear005
  Group = -> [BaseFeature001,Sketch032,Pocket019,Sketch033,Groove]
  Origin = -> Origin014
  Tip = -> Groove
COMPONENT P12 — recipe-attached ("fork-rear-plate001", modeled in this document).
Construction recipe (the document's own serialized feature program — sketch geometry with constraints, then the solid features built on it; lengths are millimeters unless a unit is written):

FEATURE [Sketcher::SketchObject] Sketch034
  ArcFitTolerance = 0
  AttachmentSupport = -> [XZ_Plane016]
  ExternalTypes = [0]
  FullyConstrained = true
  MakeInternals = false
  MapMode = 5
  Placement = pos=(0,0,0) rot=(1,0,0;1.5708rad)
  sketch-geometry (7):
    g0: LineSegment StartX=-170 StartY=0 StartZ=0 EndX=170 EndY=0 EndZ=0
    g1: LineSegment StartX=170 StartY=0 StartZ=0 EndX=170 EndY=380 EndZ=0
    g2: LineSegment StartX=170 StartY=380 StartZ=0 EndX=90 EndY=380 EndZ=0
    g3: LineSegment StartX=-170 StartY=380 StartZ=0 EndX=-170 EndY=0 EndZ=0
    g4: ArcOfCircle CenterX=0 CenterY=500 CenterZ=0 NormalX=0 NormalY=0 NormalZ=1 AngleXU=0 Radius=150 StartAngle=4.06889 EndAngle=5.35589
    g5: LineSegment StartX=-90 StartY=380 StartZ=0 EndX=-170 EndY=380 EndZ=0
    g6: GeomPoint [constr] X=0 Y=350 Z=0
  constraints (19):
    c: Coincident(g0,g1)
    c: Coincident(g1,g2)
    c: Coincident(g5,g3)
    c: Coincident(g3,g0)
    c: Horizontal(g0)
    c: Vertical(g1)
    c: Vertical(g3)
    c: PointOnObject(g0,g-1)
    c: Symmetric(g1,g5,g-2)
    c: DistanceY(g1,g1) = 380
    c: DistanceX(g0,g0) = 340
    c: Tangent(g2,g5)
    c: Coincident(g4,g5)
    c: Coincident(g4,g2)
    c: PointOnObject(g4,g-2)
    c: PointOnObject(g6,g-2)
    c: PointOnObject(g6,g4)
    c: DistanceY(g-1,g6) = 350
    c: DistanceX(g4,g2) = 180
FEATURE [PartDesign::Pad] Pad010
  AllowMultiFace = false
  Direction = (0,-1,-1.035e-13)
  Length = 18
  Length2 = 100
  Placement = pos=(0,0,0) rot=(1,0,0;1.5708rad)
  Profile = -> Sketch034
  SideType = 0
  Suppressed = false
  Type = 0
  Type2 = 0
FEATURE [PartDesign::Body] Body010  label="fork-rear-plate"
  AllowCompound = true
  Group = -> [Sketch034,Pad010]
  Origin = -> Origin016
  Tip = -> Pad010
COMPONENT P13 — recipe-attached ("fork-side-plate001", modeled in this document).
Construction recipe (the document's own serialized feature program — sketch geometry with constraints, then the solid features built on it; lengths are millimeters unless a unit is written):

FEATURE [Sketcher::SketchObject] Sketch035
  ArcFitTolerance = 0
  AttachmentSupport = -> [YZ_Plane017]
  ExternalTypes = [0]
  FullyConstrained = true
  MakeInternals = false
  MapMode = 5
  Placement = pos=(0,0,0) rot=(0.57735,0.57735,0.57735;2.0944rad)
  sketch-geometry (5):
    g0: ArcOfCircle CenterX=0 CenterY=580 CenterZ=0 NormalX=0 NormalY=0 NormalZ=1 AngleXU=0 Radius=95 StartAngle=0.495618 EndAngle=3.41262
    g1: ArcOfCircle CenterX=-765.98 CenterY=367.162 CenterZ=0 NormalX=0 NormalY=0 NormalZ=1 AngleXU=0 Radius=700 StartAngle=5.73104 EndAngle=6.55421
    g2: ArcOfCircle CenterX=-708.138 CenterY=197.162 CenterZ=0 NormalX=0 NormalY=0 NormalZ=1 AngleXU=0 Radius=900 StartAngle=6.06233 EndAngle=6.7788
    g3: LineSegment StartX=-170 StartY=-2.274e-13 StartZ=0 EndX=170 EndY=-1.705e-13 EndZ=0
    g4: Circle CenterX=0 CenterY=580 CenterZ=0 NormalX=0 NormalY=0 NormalZ=1 AngleXU=0 Radius=6
  constraints (16):
    c: PointOnObject(g0,g-2)
    c: Radius(g0) = 95
    c: DistanceY(g-1,g0) = 580
    c: PointOnObject(g1,g-1)
    c: PointOnObject(g2,g-1)
    c: Tangent(g2,g0)
    c: Coincident(g3,g1)
    c: Coincident(g3,g2)
    c: DistanceX(g3,g3) = 340
    c: DistanceX(g1,g-1) = 170
    c: Radius(g1) = 700
    c: Radius(g2) = 900
    c: Coincident(g0,g2)
    c: Tangent(g0,g1) = 1.5708
    c: Coincident(g4,g0)
    c: Radius(g4) = 6
FEATURE [PartDesign::Pad] Pad011
  AllowMultiFace = false
  Direction = (1,-1.128e-13,1.13e-13)
  Length = 18
  Length2 = 100
  Placement = pos=(0,0,0) rot=(0.57735,0.57735,0.57735;2.0944rad)
  Profile = -> Sketch035
  SideType = 2
  Suppressed = false
  Type = 0
  Type2 = 0
FEATURE [Sketcher::SketchObject] Sketch036
  ArcFitTolerance = 0
  AttachmentSupport = -> [Pad011]
  ExternalGeometry = -> [Pad011]
  ExternalTypes = [0]
  FullyConstrained = true
  MakeInternals = false
  MapMode = 5
  Placement = pos=(9,-1.0152e-12,1.0172e-12) rot=(0.57735,0.57735,0.57735;2.0944rad)
  sketch-geometry (5):
    g0: Circle [constr] CenterX=0 CenterY=580 CenterZ=0 NormalX=0 NormalY=0 NormalZ=1 AngleXU=0 Radius=75
    g1: LineSegment [constr] StartX=0 StartY=580 StartZ=0 EndX=-53.033 EndY=526.967 EndZ=0
    g2: LineSegment [constr] StartX=0 StartY=580 StartZ=0 EndX=53.033 EndY=526.967 EndZ=0
    g3: Circle CenterX=-53.033 CenterY=526.967 CenterZ=0 NormalX=0 NormalY=0 NormalZ=1 AngleXU=0 Radius=3
    g4: Circle CenterX=53.033 CenterY=526.967 CenterZ=0 NormalX=0 NormalY=0 NormalZ=1 AngleXU=0 Radius=3
  constraints (12):
    c: Coincident(g0,g-3)
    c: Coincident(g1,g0)
    c: PointOnObject(g1,g0)
    c: Coincident(g2,g0)
    c: PointOnObject(g2,g0)
    c: Angle(g1,g2) = 1.5708
    c: Angle(g1) = -2.35619
    c: Radius(g0) = 75
    c: Coincident(g3,g1)
    c: Coincident(g4,g2)
    c: Equal(g4,g3)
    c: Radius(g4) = 3
FEATURE [PartDesign::Pocket] Pocket020
  AllowMultiFace = false
  BaseFeature = -> Pad011
  Direction = (-1,1.125e-13,-1.129e-13)
  Length = 5
  Length2 = 100
  Placement = pos=(0,0,0) rot=(0.57735,0.57735,0.57735;2.0944rad)
  Profile = -> Sketch036
  SideType = 0
  Suppressed = false
  Type = 1
  Type2 = 0
FEATURE [PartDesign::Line] DatumLine
  AttacherType = Attacher::AttachEngineLine
  AttachmentSupport = -> [Pocket020]
  Length = 18
  MapMode = 19
  Placement = pos=(9,6.45244e-11,580) rot=(0.57735,0.57735,0.57735;2.0944rad)
  ResizeMode = 0
FEATURE [Sketcher::SketchObject] Sketch037
  ArcFitTolerance = 0
  AttachmentSupport = -> [Pocket020]
  ExternalGeometry = -> [Pocket020]
  ExternalTypes = [0]
  FullyConstrained = true
  MakeInternals = false
  MapMode = 5
  Placement = pos=(9,-1.0152e-12,1.0172e-12) rot=(0.57735,0.57735,0.57735;2.0944rad)
  sketch-geometry (1):
    g0: LineSegment StartX=2.416e-13 StartY=580 StartZ=0 EndX=0 EndY=0 EndZ=0
  constraints (2):
    c: Coincident(g0,g-3)
    c: Coincident(g0,g-1)
FEATURE [PartDesign::Body] Body011  label="fork-side-plate"
  AllowCompound = true
  Group = -> [Sketch035,Pad011,Sketch036,Pocket020,DatumLine,Sketch037]
  Origin = -> Origin017
  Tip = -> Pocket020
COMPONENT P14 — same part as P13; its construction recipe is shown at P13.
COMPONENT P15 — recipe-attached ("tube-main001", modeled in this document).
Construction recipe (the document's own serialized feature program — sketch geometry with constraints, then the solid features built on it; lengths are millimeters unless a unit is written):

FEATURE [Sketcher::SketchObject] Sketch059
  ArcFitTolerance = 0
  AttachmentSupport = -> [XY_Plane023]
  ExternalTypes = [0]
  FullyConstrained = true
  MakeInternals = false
  MapMode = 5
  sketch-geometry (2):
    g0: Circle CenterX=0 CenterY=0 CenterZ=0 NormalX=0 NormalY=0 NormalZ=1 AngleXU=0 Radius=140
    g1: Circle CenterX=0 CenterY=0 CenterZ=0 NormalX=0 NormalY=0 NormalZ=1 AngleXU=0 Radius=143
  constraints (4):
    c: Coincident(g0,g-1)
    c: Coincident(g1,g0)
    c: Radius(g1) = 143
    c: Radius(g0) = 140
FEATURE [PartDesign::Pad] Pad020
  AllowMultiFace = false
  Direction = (0,0,1)
  Length = 1120
  Length2 = 100
  Profile = -> Sketch059
  SideType = 0
  Suppressed = false
  Type = 0
  Type2 = 0
FEATURE [PartDesign::Plane] DatumPlane004
  AttachmentOffset = pos=(0,0,-20) rot=(0,0,1;0rad)
  AttachmentSupport = -> [Pad020]
  Length = 404.321
  MapMode = 5
  Placement = pos=(0,0,20) rot=(1,0,0;3.14159rad)
  ResizeMode = 0
  Width = 346.236
FEATURE [Sketcher::SketchObject] Sketch060
  ArcFitTolerance = 0
  AttachmentSupport = -> [DatumPlane004]
  ExternalGeometry = -> [Pad020]
  ExternalTypes = [0]
  FullyConstrained = true
  MakeInternals = false
  MapMode = 5
  Placement = pos=(0,0,20) rot=(1,0,0;3.14159rad)
  sketch-geometry (2):
    g0: Circle CenterX=0 CenterY=0 CenterZ=0 NormalX=0 NormalY=0 NormalZ=1 AngleXU=0 Radius=140
    g1: Circle CenterX=0 CenterY=0 CenterZ=0 NormalX=0 NormalY=0 NormalZ=1 AngleXU=0 Radius=103
  constraints (4):
    c: Coincident(g0,g-1)
    c: Coincident(g1,g0)
    c: Equal(g-3,g0)
    c: Radius(g1) = 103
FEATURE [PartDesign::Pad] Pad021
  AllowMultiFace = false
  BaseFeature = -> Pad020
  Direction = (0,0,-1)
  Length = 10
  Length2 = 100
  Profile = -> Sketch060
  Reversed = true
  SideType = 0
  Suppressed = false
  Type = 0
  Type2 = 0
FEATURE [PartDesign::Plane] DatumPlane005
  AttachmentOffset = pos=(0,0,150) rot=(0,0,1;0rad)
  AttachmentSupport = -> [YZ_Plane023]
  Length = 397.947
  MapMode = 5
  Placement = pos=(150,-1.69198e-11,1.69531e-11) rot=(0.57735,0.57735,0.57735;2.0944rad)
  ResizeMode = 0
  Width = 1259.03
FEATURE [Sketcher::SketchObject] Sketch061
  ArcFitTolerance = 0
  AttachmentSupport = -> [DatumPlane005]
  ExternalTypes = [0]
  FullyConstrained = true
  MakeInternals = false
  MapMode = 5
  Placement = pos=(150,-1.69198e-11,1.69531e-11) rot=(0.57735,0.57735,0.57735;2.0944rad)
  sketch-geometry (1):
    g0: Circle CenterX=0 CenterY=420 CenterZ=0 NormalX=0 NormalY=0 NormalZ=1 AngleXU=0 Radius=90
  constraints (3):
    c: PointOnObject(g0,g-2)
    c: DistanceY(g0) = 420
    c: Radius(g0) = 90
FEATURE [PartDesign::Pad] Pad022
  AllowMultiFace = false
  BaseFeature = -> Pad021
  Direction = (1,0,0)
  Length = 23
  Length2 = 100
  Profile = -> Sketch061
  ReferenceAxis = -> Sketch061 [N_Axis]
  Reversed = true
  SideType = 0
  Suppressed = false
  Type = 2
  Type2 = 0
FEATURE [Sketcher::SketchObject] Sketch062
  ArcFitTolerance = 0
  AttachmentSupport = -> [Pad022]
  ExternalTypes = [0]
  FullyConstrained = true
  MakeInternals = false
  MapMode = 5
  Placement = pos=(150,-1.6926e-11,1.6956e-11) rot=(0.57735,0.57735,0.57735;2.0944rad)
  sketch-geometry (1):
    g0: Circle CenterX=0 CenterY=420 CenterZ=0 NormalX=0 NormalY=0 NormalZ=1 AngleXU=0 Radius=65
  constraints (2):
    c: Coincident(g0,g-3)
    c: Radius(g0) = 65
FEATURE [PartDesign::Pad] Pad023
  AllowMultiFace = false
  BaseFeature = -> Pad022
  Direction = (1,-1.127e-13,1.129e-13)
  Length = 20
  Length2 = 100
  Profile = -> Sketch062
  SideType = 0
  Suppressed = false
  Type = 0
  Type2 = 0
FEATURE [Sketcher::SketchObject] Sketch063
  ArcFitTolerance = 0
  AttachmentSupport = -> [Pad023]
  ExternalGeometry = -> [Pad023]
  ExternalTypes = [0]
  FullyConstrained = true
  MakeInternals = false
  MapMode = 5
  Placement = pos=(170,-1.91539e-11,1.91845e-11) rot=(0.57735,0.57735,0.57735;2.0944rad)
  sketch-geometry (2):
    g0: Circle CenterX=0 CenterY=420 CenterZ=0 NormalX=0 NormalY=0 NormalZ=1 AngleXU=0 Radius=32
    g1: Circle CenterX=0 CenterY=420 CenterZ=0 NormalX=0 NormalY=0 NormalZ=1 AngleXU=0 Radius=25
  constraints (4):
    c: Coincident(g0,g-3)
    c: Radius(g0) = 32
    c: Coincident(g1,g0)
    c: Radius(g1) = 25
FEATURE [PartDesign::Pad] Pad024
  AllowMultiFace = false
  BaseFeature = -> Pad023
  Direction = (1,-1.126e-13,1.13e-13)
  Length = 1
  Length2 = 100
  Profile = -> Sketch063
  SideType = 0
  Suppressed = false
  Type = 0
  Type2 = 0
FEATURE [PartDesign::Plane] DatumPlane006
  AttachmentOffset = pos=(0,0,-150) rot=(0,0,1;0rad)
  AttachmentSupport = -> [YZ_Plane023]
  Length = 397.947
  MapMode = 5
  Placement = pos=(-150,1.69198e-11,-1.69531e-11) rot=(0.57735,0.57735,0.57735;2.0944rad)
  ResizeMode = 0
  Width = 1259.03
FEATURE [Sketcher::SketchObject] Sketch064
  ArcFitTolerance = 0
  AttachmentSupport = -> [DatumPlane006]
  ExternalGeometry = -> [Pad024]
  ExternalTypes = [0]
  FullyConstrained = true
  MakeInternals = false
  MapMode = 5
  Placement = pos=(-150,1.69198e-11,-1.69531e-11) rot=(0.57735,0.57735,0.57735;2.0944rad)
  sketch-geometry (1):
    g0: Circle CenterX=0 CenterY=420 CenterZ=0 NormalX=0 NormalY=0 NormalZ=1 AngleXU=0 Radius=90
  constraints (2):
    c: Coincident(g0,g-3)
    c: Equal(g0,g-3)
FEATURE [PartDesign::Pad] Pad025
  AllowMultiFace = false
  BaseFeature = -> Pad024
  Direction = (1,-1.128e-13,1.13e-13)
  Length = 10
  Length2 = 100
  Profile = -> Sketch064
  SideType = 0
  Suppressed = false
  Type = 3
  Type2 = 0
  UpToFace = -> Pad024 [Face1]
FEATURE [Sketcher::SketchObject] Sketch065
  ArcFitTolerance = 0
  AttachmentSupport = -> [Pad025]
  ExternalGeometry = -> [Pad025]
  ExternalTypes = [0]
  FullyConstrained = true
  MakeInternals = false
  MapMode = 5
  Placement = pos=(-150,1.6926e-11,-1.6956e-11) rot=(-0.57735,0.57735,0.57735;4.18879rad)
  sketch-geometry (1):
    g0: Circle CenterX=0 CenterY=420 CenterZ=0 NormalX=0 NormalY=0 NormalZ=1 AngleXU=0 Radius=65
  constraints (2):
    c: Coincident(g0,g-3)
    c: Equal(g-4,g0)
FEATURE [PartDesign::Pad] Pad026
  AllowMultiFace = false
  BaseFeature = -> Pad025
  Direction = (-1,1.127e-13,-1.129e-13)
  Length = 20
  Length2 = 100
  Profile = -> Sketch065
  SideType = 0
  Suppressed = false
  Type = 0
  Type2 = 0
FEATURE [Sketcher::SketchObject] Sketch066
  ArcFitTolerance = 0
  AttachmentSupport = -> [Pad026]
  ExternalGeometry = -> [Pad026]
  ExternalTypes = [0]
  FullyConstrained = true
  MakeInternals = false
  MapMode = 5
  Placement = pos=(-170,1.91539e-11,-1.91845e-11) rot=(-0.57735,0.57735,0.57735;4.18879rad)
  sketch-geometry (2):
    g0: Circle CenterX=0 CenterY=420 CenterZ=0 NormalX=0 NormalY=0 NormalZ=1 AngleXU=0 Radius=25
    g1: Circle CenterX=0 CenterY=420 CenterZ=0 NormalX=0 NormalY=0 NormalZ=1 AngleXU=0 Radius=32
  constraints (4):
    c: Coincident(g0,g-4)
    c: Coincident(g1,g0)
    c: Equal(g1,g-3)
    c: Equal(g0,g-4)
FEATURE [PartDesign::Pad] Pad027
  AllowMultiFace = false
  BaseFeature = -> Pad026
  Direction = (-1,1.126e-13,-1.13e-13)
  Length = 1
  Length2 = 100
  Profile = -> Sketch066
  SideType = 0
  Suppressed = false
  Type = 0
  Type2 = 0
FEATURE [Sketcher::SketchObject] Sketch067
  ArcFitTolerance = 0
  AttachmentSupport = -> [Pad027]
  ExternalGeometry = -> [Pad027]
  ExternalTypes = [0]
  FullyConstrained = true
  MakeInternals = false
  MapMode = 5
  Placement = pos=(170,-1.91539e-11,1.91845e-11) rot=(0.57735,0.57735,0.57735;2.0944rad)
  sketch-geometry (1):
    g0: Circle CenterX=0 CenterY=420 CenterZ=0 NormalX=0 NormalY=0 NormalZ=1 AngleXU=0 Radius=5.25
  constraints (2):
    c: Coincident(g0,g-3)
    c: Radius(g0) = 5.25
FEATURE [PartDesign::Pocket] Pocket033
  AllowMultiFace = false
  BaseFeature = -> Pad027
  Direction = (-1,1.126e-13,-1.13e-13)
  Length = 7
  Length2 = 100
  Profile = -> Sketch067
  SideType = 0
  Suppressed = false
  Type = 0
  Type2 = 0
FEATURE [Sketcher::SketchObject] Sketch068
  ArcFitTolerance = 0
  AttachmentSupport = -> [Pocket033]
  ExternalGeometry = -> [Pocket033]
  ExternalTypes = [0]
  FullyConstrained = true
  MakeInternals = false
  MapMode = 5
  Placement = pos=(163,-1.85315e-11,1.8851e-11) rot=(0.57735,0.57735,0.57735;2.0944rad)
  sketch-geometry (1):
    g0: Circle CenterX=0 CenterY=420 CenterZ=0 NormalX=0 NormalY=0 NormalZ=1 AngleXU=0 Radius=4.25
  constraints (2):
    c: Coincident(g0,g-3)
    c: Radius(g0) = 4.25
FEATURE [PartDesign::Pocket] Pocket034
  AllowMultiFace = false
  BaseFeature = -> Pocket033
  Direction = (-1,1.136e-13,-1.156e-13)
  Length = 15
  Length2 = 100
  Profile = -> Sketch068
  SideType = 0
  Suppressed = false
  Type = 0
  Type2 = 0
FEATURE [Sketcher::SketchObject] Sketch069
  ArcFitTolerance = 0
  AttachmentSupport = -> [Pocket034]
  ExternalGeometry = -> [Pocket034]
  ExternalTypes = [0]
  FullyConstrained = true
  MakeInternals = false
  MapMode = 5
  Placement = pos=(-170,1.91539e-11,-1.91845e-11) rot=(-0.57735,0.57735,0.57735;4.18879rad)
  sketch-geometry (1):
    g0: Circle CenterX=0 CenterY=420 CenterZ=0 NormalX=0 NormalY=0 NormalZ=1 AngleXU=0 Radius=5.25
  constraints (2):
    c: Coincident(g0,g-3)
    c: Radius(g0) = 5.25
FEATURE [PartDesign::Pocket] Pocket035
  AllowMultiFace = false
  BaseFeature = -> Pocket034
  Direction = (1,-1.126e-13,1.13e-13)
  Length = 7
  Length2 = 100
  Profile = -> Sketch069
  SideType = 0
  Suppressed = false
  Type = 0
  Type2 = 0
FEATURE [Sketcher::SketchObject] Sketch070
  ArcFitTolerance = 0
  AttachmentSupport = -> [Pocket035]
  ExternalGeometry = -> [Pocket035]
  ExternalTypes = [0]
  FullyConstrained = true
  MakeInternals = false
  MapMode = 5
  Placement = pos=(-163,1.82364e-11,-1.83408e-11) rot=(-0.57735,0.57735,0.57735;4.18879rad)
  sketch-geometry (1):
    g0: Circle CenterX=0 CenterY=420 CenterZ=0 NormalX=0 NormalY=0 NormalZ=1 AngleXU=0 Radius=4.25
  constraints (2):
    c: Coincident(g0,g-3)
    c: Radius(g0) = 4.25
FEATURE [PartDesign::Pocket] Pocket036
  AllowMultiFace = false
  BaseFeature = -> Pocket035
  Direction = (1,-1.118e-13,1.125e-13)
  Length = 15
  Length2 = 100
  Profile = -> Sketch070
  SideType = 0
  Suppressed = false
  Type = 0
  Type2 = 0
FEATURE [PartDesign::Body] Body014  label="tube-main"
  AllowCompound = true
  Group = -> [Sketch059,Pad020,DatumPlane004,Sketch060,Pad021,DatumPlane005,Sketch061,Pad022,Sketch062,Pad023,Sketch063,Pad024,DatumPlane006,Sketch064,Pad025,Sketch065,Pad026,Sketch066,Pad027,Sketch067,Pocket033,Sketch068,Pocket034,Sketch069,Pocket035,Sketch070,Pocket036]
  Origin = -> Origin023
  Tip = -> Pocket036
COMPONENT P16 — recipe-attached ("tube-main-gear001", modeled in this document).
Construction recipe (the document's own serialized feature program — sketch geometry with constraints, then the solid features built on it; lengths are millimeters unless a unit is written):

FEATURE [Sketcher::SketchObject] Sketch051
  ArcFitTolerance = 0
  AttachmentSupport = -> [XZ_Plane020]
  ExternalTypes = [0]
  FullyConstrained = true
  MakeInternals = false
  MapMode = 5
  Placement = pos=(0,0,0) rot=(1,0,0;1.5708rad)
  sketch-geometry (2):
    g0: Circle CenterX=0 CenterY=-135 CenterZ=0 NormalX=0 NormalY=0 NormalZ=1 AngleXU=0 Radius=145
    g1: GeomPoint [constr] X=0 Y=10 Z=0
  constraints (5):
    c: PointOnObject(g0,g-2)
    c: PointOnObject(g1,g0)
    c: PointOnObject(g1,g-2)
    c: DistanceY(g-1,g1) = 10
    c: Diameter(g0) = 290
FEATURE [Sketcher::SketchObject] Sketch052
  ArcFitTolerance = 0
  AttachmentSupport = -> [XY_Plane020]
  ExternalTypes = [0]
  FullyConstrained = true
  MakeInternals = false
  MapMode = 5
  sketch-geometry (4):
    g0: LineSegment StartX=-150 StartY=-20 StartZ=0 EndX=150 EndY=-20 EndZ=0
    g1: LineSegment StartX=150 StartY=-20 StartZ=0 EndX=150 EndY=-170 EndZ=0
    g2: LineSegment StartX=150 StartY=-170 StartZ=0 EndX=-150 EndY=-170 EndZ=0
    g3: LineSegment StartX=-150 StartY=-170 StartZ=0 EndX=-150 EndY=-20 EndZ=0
  constraints (11):
    c: Coincident(g0,g1)
    c: Coincident(g1,g2)
    c: Coincident(g2,g3)
    c: Coincident(g3,g0)
    c: Horizontal(g2)
    c: Vertical(g1)
    c: Vertical(g3)
    c: DistanceY(g0,g-1) = 20
    c: Symmetric(g0,g0,g-2)
    c: DistanceX(g2,g2) = 300
    c: DistanceY(g1,g1) = 150
FEATURE [PartDesign::Plane] DatumPlane003
  AttachmentOffset = pos=(0,0,5) rot=(0,0,1;0rad)
  AttachmentSupport = -> [XY_Plane020]
  Length = 249.689
  MapMode = 5
  Placement = pos=(0,0,5) rot=(0,0,1;0rad)
  ResizeMode = 0
  Width = 194.689
FEATURE [Sketcher::SketchObject] Sketch053
  ArcFitTolerance = 0
  AttachmentSupport = -> [DatumPlane003]
  ExternalTypes = [0]
  FullyConstrained = true
  MakeInternals = false
  MapMode = 5
  Placement = pos=(0,0,5) rot=(0,0,1;0rad)
  sketch-geometry (6):
    g0: LineSegment StartX=80 StartY=0 StartZ=0 EndX=80 EndY=2 EndZ=0
    g1: LineSegment StartX=80 StartY=2 StartZ=0 EndX=98 EndY=2 EndZ=0
    g2: LineSegment StartX=98 StartY=2 StartZ=0 EndX=98 EndY=3.5 EndZ=0
    g3: LineSegment StartX=98 StartY=3.5 StartZ=0 EndX=140 EndY=3.5 EndZ=0
    g4: LineSegment StartX=140 StartY=3.5 StartZ=0 EndX=140 EndY=0 EndZ=0
    g5: LineSegment StartX=140 StartY=0 StartZ=0 EndX=80 EndY=0 EndZ=0
  constraints (18):
    c: PointOnObject(g0,g-1)
    c: Vertical(g0)
    c: Coincident(g0,g1)
    c: Horizontal(g1)
    c: Coincident(g1,g2)
    c: Coincident(g2,g3)
    c: Horizontal(g3)
    c: Coincident(g3,g4)
    c: PointOnObject(g4,g-1)
    c: Vertical(g4)
    c: Coincident(g4,g5)
    c: Coincident(g5,g0)
    c: DistanceX(g0) = 80
    c: DistanceX(g1,g1) = 18
    c: Vertical(g2)
    c: DistanceY(g0,g0) = 2
    c: DistanceY(g4,g4) = 3.5
    c: DistanceX(g5,g5) = 60
FEATURE [PartDesign::PolarPattern] PolarPattern004
  Angle = 45
  Axis = -> Z_Axis020
  Mode = 0
  Occurrences = 3
  Offset = 120
  SpacingPattern = [0]
  Spacings = [-1,-1]
  Suppressed = false
  TransformMode = 0
FEATURE [PartDesign::Mirrored] Mirrored
  MirrorPlane = -> YZ_Plane020
  Suppressed = false
  TransformMode = 0
FEATURE [Sketcher::SketchObject] Sketch054
  ArcFitTolerance = 0
  AttachmentSupport = -> [XY_Plane020]
  ExternalTypes = [0]
  FullyConstrained = true
  MakeInternals = false
  MapMode = 5
  sketch-geometry (4):
    g0: LineSegment StartX=160 StartY=150 StartZ=0 EndX=10 EndY=0 EndZ=0
    g1: LineSegment StartX=10 StartY=0 StartZ=0 EndX=10 EndY=-30 EndZ=0
    g2: LineSegment StartX=10 StartY=-30 StartZ=0 EndX=160 EndY=-30 EndZ=0
    g3: LineSegment StartX=160 StartY=-30 StartZ=0 EndX=160 EndY=150 EndZ=0
  constraints (12):
    c: PointOnObject(g0,g-1)
    c: Coincident(g0,g1)
    c: Vertical(g1)
    c: Coincident(g1,g2)
    c: Horizontal(g2)
    c: Coincident(g2,g3)
    c: Coincident(g3,g0)
    c: Angle(g-1,g0) = 0.785398
    c: DistanceX(g0) = 10
    c: Vertical(g3)
    c: DistanceY(g2) = -30
    c: DistanceX(g2,g2) = 150
FEATURE [Sketcher::SketchObject] Sketch055
  ArcFitTolerance = 0
  AttachmentSupport = -> [XY_Plane020]
  ExternalTypes = [0]
  FullyConstrained = true
  MakeInternals = false
  MapMode = 5
  sketch-geometry (5):
    g0: LineSegment StartX=-92 StartY=8 StartZ=0 EndX=-97 EndY=8 EndZ=0
    g1: ArcOfCircle CenterX=0 CenterY=0 CenterZ=0 NormalX=0 NormalY=0 NormalZ=1 AngleXU=0 Radius=92.3472 StartAngle=2.82743 EndAngle=3.05485
    g2: ArcOfCircle CenterX=0 CenterY=0 CenterZ=0 NormalX=0 NormalY=0 NormalZ=1 AngleXU=0 Radius=97.3293 StartAngle=2.82743 EndAngle=3.0593
    g3: LineSegment StartX=-92.5657 StartY=30.0764 StartZ=0 EndX=-87.8274 EndY=28.5368 EndZ=0
    g4: LineSegment [constr] StartX=-87.8274 StartY=28.5368 StartZ=0 EndX=0 EndY=0 EndZ=0
  constraints (14):
    c: Horizontal(g0)
    c: Coincident(g1,g-1)
    c: Coincident(g1,g0)
    c: Coincident(g2,g1)
    c: Coincident(g2,g0)
    c: Coincident(g3,g2)
    c: Coincident(g3,g1)
    c: DistanceX(g0) = -92
    c: DistanceY(g0) = 8
    c: DistanceX(g0,g0) = 5
    c: Angle(g3,g0) = 0.314159
    c: Coincident(g4,g1)
    c: Coincident(g4,g1)
    c: Parallel(g4,g3)
FEATURE [Sketcher::SketchObject] Sketch056
  ArcFitTolerance = 0
  AttachmentSupport = -> [XY_Plane020]
  ExternalTypes = [0]
  FullyConstrained = true
  MakeInternals = false
  MapMode = 5
  sketch-geometry (2):
    g0: Circle CenterX=0 CenterY=0 CenterZ=0 NormalX=0 NormalY=0 NormalZ=1 AngleXU=0 Radius=100
    g1: Circle CenterX=0 CenterY=0 CenterZ=0 NormalX=0 NormalY=0 NormalZ=1 AngleXU=0 Radius=150
  constraints (4):
    c: Coincident(g0,g-1)
    c: Coincident(g1,g0)
    c: Diameter(g0) = 200
    c: Diameter(g1) = 300
FEATURE [Sketcher::SketchObject] Sketch057
  ArcFitTolerance = 0
  AttachmentSupport = -> [XY_Plane020]
  ExternalTypes = [0]
  FullyConstrained = true
  MakeInternals = false
  MapMode = 5
  sketch-geometry (1):
    g0: Circle CenterX=-115 CenterY=0 CenterZ=0 NormalX=0 NormalY=0 NormalZ=1 AngleXU=0 Radius=11
  constraints (3):
    c: PointOnObject(g0,g-1)
    c: DistanceX(g0) = -115
    c: Diameter(g0) = 22
FEATURE [Sketcher::SketchObject] Sketch058
  ArcFitTolerance = 0
  AttachmentSupport = -> [XY_Plane020]
  ExternalTypes = [0]
  FullyConstrained = true
  MakeInternals = false
  MapMode = 5
  sketch-geometry (4):
    g0: LineSegment StartX=80 StartY=120 StartZ=0 EndX=160 EndY=120 EndZ=0
    g1: LineSegment StartX=160 StartY=120 StartZ=0 EndX=160 EndY=0 EndZ=0
    g2: LineSegment StartX=160 StartY=0 StartZ=0 EndX=80 EndY=0 EndZ=0
    g3: LineSegment StartX=80 StartY=0 StartZ=0 EndX=80 EndY=120 EndZ=0
  constraints (12):
    c: Coincident(g0,g1)
    c: Coincident(g1,g2)
    c: Coincident(g2,g3)
    c: Coincident(g3,g0)
    c: Horizontal(g0)
    c: Horizontal(g2)
    c: Vertical(g1)
    c: Vertical(g3)
    c: PointOnObject(g1,g-1)
    c: DistanceX(g2) = 80
    c: DistanceY(g1,g1) = 120
    c: DistanceX(g2,g2) = 80
FEATURE [PartDesign::FeatureBase] BaseFeature002
  BaseFeature = -> InvoluteGear
  Suppressed = false
FEATURE [Sketcher::SketchObject] Sketch050
  ArcFitTolerance = 0
  AttachmentSupport = -> [BaseFeature002]
  ExternalTypes = [0]
  FullyConstrained = true
  MakeInternals = false
  MapMode = 5
  Placement = pos=(0,0,29) rot=(0,0,1;0rad)
  sketch-geometry (1):
    g0: Circle CenterX=0 CenterY=0 CenterZ=0 NormalX=0 NormalY=0 NormalZ=1 AngleXU=0 Radius=90
  constraints (2):
    c: Coincident(g0,g-1)
    c: Diameter(g0) = 180
FEATURE [PartDesign::Pocket] Pocket025  label="Pocket025-mount-diameter"
  BaseFeature = -> BaseFeature002
  Direction = (0,0,-1)
  Length = 5
  Length2 = 100
  Profile = -> Sketch050
  SideType = 0
  Suppressed = false
  Type = 1
  Type2 = 0
FEATURE [PartDesign::Pocket] Pocket026  label="Pocket026-tube-diameter"
  BaseFeature = -> Pocket025
  Direction = (0,1,-2e-16)
  Length = 5
  Length2 = 100
  Profile = -> Sketch051
  SideType = 2
  Suppressed = false
  Type = 1
  Type2 = 0
FEATURE [PartDesign::Pocket] Pocket027
  BaseFeature = -> Pocket026
  Direction = (0,0,-1)
  Length = 5
  Length2 = 100
  Profile = -> Sketch052
  Reversed = true
  SideType = 0
  Suppressed = false
  Type = 1
  Type2 = 0
FEATURE [PartDesign::Groove] Groove001
  Angle = 360
  Angle2 = 60
  Axis = (1,0,0)
  Base = (0,0,5)
  BaseFeature = -> Pocket027
  Profile = -> Sketch053
  ReferenceAxis = -> Sketch053 [H_Axis]
  Reversed = true
  Suppressed = false
  Type = 0
FEATURE [PartDesign::MultiTransform] MultiTransform001
  BaseFeature = -> Groove001
  Originals = -> [Groove001]
  Suppressed = false
  TransformMode = 0
  Transformations = -> [PolarPattern004,Mirrored]
FEATURE [PartDesign::Pocket] Pocket028
  BaseFeature = -> MultiTransform001
  Direction = (0,0,-1)
  Length = 5
  Length2 = 100
  Profile = -> Sketch054
  Reversed = true
  SideType = 0
  Suppressed = false
  Type = 1
  Type2 = 0
FEATURE [PartDesign::Pocket] Pocket029
  BaseFeature = -> Pocket028
  Direction = (0,0,-1)
  Length = 5
  Length2 = 100
  Profile = -> Sketch055
  Reversed = true
  SideType = 0
  Suppressed = false
  Type = 1
  Type2 = 0
FEATURE [PartDesign::PolarPattern] PolarPattern005
  Angle = 112
  Axis = -> Z_Axis020
  BaseFeature = -> Pocket029
  Mode = 0
  Occurrences = 6
  Offset = 120
  Originals = -> [Pocket029]
  Reversed = true
  SpacingPattern = [0]
  Spacings = [-1,-1,-1,-1,-1]
  Suppressed = false
  TransformMode = 0
FEATURE [PartDesign::Pocket] Pocket030
  BaseFeature = -> PolarPattern005
  Direction = (0,0,-1)
  Length = 20
  Length2 = 100
  Profile = -> Sketch056
  ReferenceAxis = -> Sketch056 [N_Axis]
  Reversed = true
  SideType = 0
  Suppressed = false
  Type = 0
  Type2 = 0
FEATURE [PartDesign::Fillet] Fillet003
  Base = -> Pocket030 [Edge44]
  BaseFeature = -> Pocket030
  Radius = 3
  SupportTransform = true
  Suppressed = false
  UseAllEdges = false
FEATURE [PartDesign::Pocket] Pocket031
  BaseFeature = -> Fillet003
  Direction = (0,0,-1)
  Length = 5
  Length2 = 100
  Profile = -> Sketch057
  Reversed = true
  SideType = 0
  Suppressed = false
  Type = 1
  Type2 = 0
FEATURE [PartDesign::PolarPattern] PolarPattern006
  Angle = 120
  Axis = -> Sketch057 [N_Axis]
  BaseFeature = -> Pocket031
  Mode = 0
  Occurrences = 10
  Offset = 120
  Originals = -> [Pocket031]
  Reversed = true
  SpacingPattern = [0]
  Spacings = [-1,-1,-1,-1,-1,-1,-1,-1,-1]
  Suppressed = false
  TransformMode = 0
FEATURE [PartDesign::Pocket] Pocket032
  BaseFeature = -> PolarPattern006
  Direction = (0,0,-1)
  Length = 5
  Length2 = 100
  Profile = -> Sketch058
  Reversed = true
  SideType = 0
  Suppressed = false
  Type = 1
  Type2 = 0
FEATURE [PartDesign::Body] Body013  label="tube-gear"
  AllowCompound = true
  Group = -> [BaseFeature002,Sketch050,Pocket025,Sketch051,Pocket026,Sketch052,Pocket027,DatumPlane003,Sketch053,Groove001,MultiTransform001,PolarPattern004,Mirrored,Sketch054,Pocket028,Sketch055,Pocket029,PolarPattern005,Sketch056,Pocket030,Fillet003,Sketch057,Pocket031,PolarPattern006,Sketch058,Pocket032]
  Origin = -> Origin020
  Tip = -> Pocket032
COMPONENT P17 — recipe-attached ("tube-gearbox-body001", modeled in this document).
Construction recipe (the document's own serialized feature program — sketch geometry with constraints, then the solid features built on it; lengths are millimeters unless a unit is written):

FEATURE [Sketcher::SketchObject] Sketch071
  ArcFitTolerance = 0
  AttachmentSupport = -> [XY_Plane024]
  ExternalTypes = [0]
  FullyConstrained = true
  MakeInternals = false
  MapMode = 5
  sketch-geometry (7):
    g0: LineSegment StartX=-65 StartY=-80 StartZ=0 EndX=37 EndY=-80 EndZ=0
    g1: LineSegment StartX=37 StartY=-80 StartZ=0 EndX=37 EndY=25 EndZ=0
    g2: LineSegment StartX=37 StartY=25 StartZ=0 EndX=-65 EndY=25 EndZ=0
    g3: LineSegment StartX=-65 StartY=25 StartZ=0 EndX=-65 EndY=-80 EndZ=0
    g4: Circle CenterX=2 CenterY=0 CenterZ=0 NormalX=0 NormalY=0 NormalZ=1 AngleXU=0 Radius=11
    g5: Circle CenterX=-40 CenterY=-4e-15 CenterZ=0 NormalX=0 NormalY=0 NormalZ=1 AngleXU=0 Radius=13.5
    g6: LineSegment [constr] StartX=2 StartY=0 StartZ=0 EndX=-40 EndY=-4e-15 EndZ=0
  constraints (20):
    c: Coincident(g0,g1)
    c: Coincident(g1,g2)
    c: Coincident(g2,g3)
    c: Coincident(g3,g0)
    c: Horizontal(g0)
    c: Horizontal(g2)
    c: Vertical(g1)
    c: Vertical(g3)
    c: DistanceX(g0) = -65
    c: DistanceY(g0) = -80
    c: DistanceY(g3,g3) = 105
    c: DistanceX(g2,g2) = 102
    c: Diameter(g4) = 22
    c: Coincident(g6,g4)
    c: Coincident(g6,g5)
    c: Diameter(g5) = 27
    c: Angle(g-1,g6) = 3.14159
    c: DistanceX(g5) = -40
    c: DistanceX(g4) = 2
    c: PointOnObject(g4,g-1)
FEATURE [PartDesign::Pad] Pad028
  Direction = (0,0,1)
  Length = 20
  Length2 = 100
  Profile = -> Sketch071
  SideType = 0
  Suppressed = false
  Type = 0
  Type2 = 0
FEATURE [Sketcher::SketchObject] Sketch072
  ArcFitTolerance = 0
  AttachmentSupport = -> [Pad028]
  ExternalGeometry = -> [Pad028]
  ExternalTypes = [0]
  FullyConstrained = true
  MakeInternals = false
  MapMode = 5
  Placement = pos=(0,0,20) rot=(0,0,1;0rad)
  sketch-geometry (4):
    g0: LineSegment StartX=37 StartY=-80 StartZ=0 EndX=-65 EndY=-80 EndZ=0
    g1: LineSegment StartX=-65 StartY=-80 StartZ=0 EndX=-65 EndY=-25 EndZ=0
    g2: LineSegment StartX=-65 StartY=-25 StartZ=0 EndX=37 EndY=-25 EndZ=0
    g3: LineSegment StartX=37 StartY=-25 StartZ=0 EndX=37 EndY=-80 EndZ=0
  constraints (11):
    c: Coincident(g0,g1)
    c: Coincident(g1,g2)
    c: Coincident(g2,g3)
    c: Coincident(g3,g0)
    c: Horizontal(g0)
    c: Horizontal(g2)
    c: Vertical(g1)
    c: Vertical(g3)
    c: Coincident(g0,g-3)
    c: PointOnObject(g1,g-4)
    c: DistanceY(g2) = -25
FEATURE [PartDesign::Pocket] Pocket037
  BaseFeature = -> Pad028
  Direction = (0,0,-1)
  Length = 10
  Length2 = 100
  Profile = -> Sketch072
  SideType = 0
  Suppressed = false
  Type = 0
  Type2 = 0
FEATURE [Sketcher::SketchObject] Sketch073
  ArcFitTolerance = 0
  AttachmentSupport = -> [Pocket037]
  ExternalTypes = [0]
  FullyConstrained = true
  MakeInternals = false
  MapMode = 5
  Placement = pos=(0,0,0) rot=(1,0,0;3.14159rad)
  sketch-geometry (5):
    g0: LineSegment StartX=23 StartY=21 StartZ=0 EndX=-19 EndY=21 EndZ=0
    g1: LineSegment StartX=-19 StartY=21 StartZ=0 EndX=-19 EndY=-21 EndZ=0
    g2: LineSegment StartX=-19 StartY=-21 StartZ=0 EndX=23 EndY=-21 EndZ=0
    g3: LineSegment StartX=23 StartY=-21 StartZ=0 EndX=23 EndY=21 EndZ=0
    g4: Circle [constr] CenterX=2 CenterY=0 CenterZ=0 NormalX=0 NormalY=0 NormalZ=1 AngleXU=0 Radius=29.6985
  constraints (15):
    c: Coincident(g0,g1)
    c: Coincident(g1,g2)
    c: Coincident(g2,g3)
    c: Coincident(g3,g0)
    c: Equal(g0,g1)
    c: Equal(g0,g2)
    c: Equal(g0,g3)
    c: PointOnObject(g0,g4)
    c: PointOnObject(g1,g4)
    c: PointOnObject(g2,g4)
    c: PointOnObject(g3,g4)
    c: Horizontal(g0)
    c: DistanceX(g0,g0) = 42
    c: PointOnObject(g4,g-1)
    c: DistanceX(g-1,g4) = 2
FEATURE [PartDesign::Pocket] Pocket038
  BaseFeature = -> Pocket037
  Direction = (0,0,1)
  Length = 16
  Length2 = 100
  Profile = -> Sketch073
  SideType = 0
  Suppressed = false
  Type = 0
  Type2 = 0
FEATURE [Sketcher::SketchObject] Sketch074
  ArcFitTolerance = 0
  AttachmentSupport = -> [Pocket038]
  ExternalTypes = [0]
  FullyConstrained = true
  MakeInternals = false
  MapMode = 5
  Placement = pos=(0,0,0) rot=(1,0,0;3.14159rad)
  sketch-geometry (4):
    g0: ArcOfCircle CenterX=28 CenterY=35 CenterZ=0 NormalX=0 NormalY=0 NormalZ=1 AngleXU=0 Radius=2 StartAngle=3.14159 EndAngle=6.28319
    g1: ArcOfCircle CenterX=28 CenterY=45 CenterZ=0 NormalX=0 NormalY=0 NormalZ=1 AngleXU=0 Radius=2 StartAngle=0 EndAngle=3.14159
    g2: LineSegment StartX=30 StartY=35 StartZ=0 EndX=30 EndY=45 EndZ=0
    g3: LineSegment StartX=26 StartY=35 StartZ=0 EndX=26 EndY=45 EndZ=0
  constraints (10):
    c: Tangent(g0,g3) = 1.5708
    c: Tangent(g0,g2) = -1.5708
    c: Tangent(g2,g1) = -1.5708
    c: Tangent(g3,g1) = 1.5708
    c: Vertical(g2)
    c: Equal(g0,g1)
    c: Radius(g0) = 2
    c: DistanceY(g2,g2) = 10
    c: DistanceX(g0) = 28
    c: DistanceY(g0) = 35
FEATURE [PartDesign::Pocket] Pocket039
  BaseFeature = -> Pocket038
  Direction = (0,0,1)
  Length = 5
  Length2 = 100
  Profile = -> Sketch074
  SideType = 0
  Suppressed = false
  Type = 1
  Type2 = 0
FEATURE [PartDesign::LinearPattern] LinearPattern002
  Direction = -> Sketch074 [H_Axis]
  Length = 84
  Length2 = 100
  Mode = 0
  Mode2 = 0
  Occurrences = 4
  Occurrences2 = 1
  Offset = 28
  Offset2 = 10
  Reversed = true
  Reversed2 = false
  SpacingPattern = [0]
  SpacingPattern2 = [0]
  Spacings = [-1,-1,-1]
  Suppressed = false
  TransformMode = 0
FEATURE [PartDesign::LinearPattern] LinearPattern003
  Direction = -> Sketch074 [V_Axis]
  Length = 30
  Length2 = 100
  Mode = 0
  Mode2 = 0
  Occurrences = 2
  Occurrences2 = 1
  Offset = 30
  Offset2 = 10
  Reversed2 = false
  SpacingPattern = [0]
  SpacingPattern2 = [0]
  Spacings = [-1]
  Suppressed = false
  TransformMode = 0
FEATURE [PartDesign::MultiTransform] MultiTransform002
  BaseFeature = -> Pocket039
  Originals = -> [Pocket039]
  Suppressed = false
  TransformMode = 0
  Transformations = -> [LinearPattern002,LinearPattern003]
FEATURE [Sketcher::SketchObject] Sketch075
  ArcFitTolerance = 0
  AttachmentSupport = -> [MultiTransform002]
  ExternalTypes = [0]
  FullyConstrained = true
  MakeInternals = false
  MapMode = 5
  Placement = pos=(0,0,16) rot=(1,0,0;3.14159rad)
  sketch-geometry (4):
    g0: Circle CenterX=16.5 CenterY=15.5 CenterZ=0 NormalX=0 NormalY=0 NormalZ=1 AngleXU=0 Radius=1.6
    g1: Circle CenterX=16.5 CenterY=-15.5 CenterZ=0 NormalX=0 NormalY=0 NormalZ=1 AngleXU=0 Radius=1.6
    g2: Circle CenterX=-14.5 CenterY=-15.5 CenterZ=0 NormalX=0 NormalY=0 NormalZ=1 AngleXU=0 Radius=1.6
    g3: Circle CenterX=-14.5 CenterY=15.5 CenterZ=0 NormalX=0 NormalY=0 NormalZ=1 AngleXU=0 Radius=1.6
  constraints (11):
    c: Equal(g0,g3)
    c: Equal(g3,g1)
    c: Equal(g1,g2)
    c: Diameter(g1) = 3.2
    c: DistanceY(g1,g0) = 31
    c: Vertical(g2,g3)
    c: Horizontal(g3,g0)
    c: Horizontal(g2,g1)
    c: DistanceX(g1) = 16.5
    c: DistanceX(g2,g1) = 31
    c: Symmetric(g0,g1,g-1)
FEATURE [PartDesign::Pocket] Pocket040
  BaseFeature = -> MultiTransform002
  Direction = (0,0,1)
  Length = 5
  Length2 = 100
  Profile = -> Sketch075
  SideType = 0
  Suppressed = false
  Type = 1
  Type2 = 0
FEATURE [PartDesign::Chamfer] Chamfer006
  Angle = 45
  Base = -> Pocket040 [Edge4,Edge2]
  BaseFeature = -> Pocket040
  ChamferType = 0
  FlipDirection = false
  Size = 5
  Size2 = 1
  SupportTransform = true
  Suppressed = false
  UseAllEdges = false
FEATURE [PartDesign::Chamfer] Chamfer007
  Angle = 45
  Base = -> Chamfer006 [Edge91,Edge89,Edge88]
  BaseFeature = -> Chamfer006
  ChamferType = 0
  FlipDirection = false
  Size = 10
  Size2 = 1
  SupportTransform = true
  Suppressed = false
  UseAllEdges = false
FEATURE [PartDesign::Fillet] Fillet004
  Base = -> Chamfer007 [Edge55]
  BaseFeature = -> Chamfer007
  Radius = 20
  SupportTransform = true
  Suppressed = false
  UseAllEdges = false
FEATURE [Sketcher::SketchObject] Sketch076
  ArcFitTolerance = 0
  AttachmentSupport = -> [Fillet004]
  ExternalGeometry = -> [Fillet004]
  ExternalTypes = [0]
  FullyConstrained = true
  MakeInternals = false
  MapMode = 5
  Placement = pos=(0,0,20) rot=(0,0,1;0rad)
  sketch-geometry (1):
    g0: Circle CenterX=-40 CenterY=-4.25258e-11 CenterZ=0 NormalX=0 NormalY=0 NormalZ=1 AngleXU=0 Radius=16
  constraints (2):
    c: Coincident(g0,g-3)
    c: Diameter(g0) = 32
FEATURE [PartDesign::Pocket] Pocket041
  BaseFeature = -> Fillet004
  Direction = (0,0,-1)
  Length = 16
  Length2 = 100
  Profile = -> Sketch076
  SideType = 0
  Suppressed = false
  Type = 0
  Type2 = 0
FEATURE [Sketcher::SketchObject] Sketch077
  ArcFitTolerance = 0
  AttachmentSupport = -> [Pocket041]
  ExternalGeometry = -> [Pocket041]
  ExternalTypes = [0]
  FullyConstrained = true
  MakeInternals = false
  MapMode = 5
  Placement = pos=(0,0,20) rot=(0,0,1;0rad)
  sketch-geometry (4):
    g0: Circle CenterX=16.5 CenterY=15.5 CenterZ=0 NormalX=0 NormalY=0 NormalZ=1 AngleXU=0 Radius=3
    g1: Circle CenterX=-14.5 CenterY=15.5 CenterZ=0 NormalX=0 NormalY=0 NormalZ=1 AngleXU=0 Radius=3
    g2: Circle CenterX=-14.5 CenterY=-15.5 CenterZ=0 NormalX=0 NormalY=0 NormalZ=1 AngleXU=0 Radius=3
    g3: Circle CenterX=16.5 CenterY=-15.5 CenterZ=0 NormalX=0 NormalY=0 NormalZ=1 AngleXU=0 Radius=3
  constraints (8):
    c: Diameter(g3) = 6
    c: Equal(g3,g2)
    c: Equal(g3,g1)
    c: Equal(g3,g0)
    c: Coincident(g2,g-6)
    c: Coincident(g3,g-5)
    c: Coincident(g0,g-4)
    c: Coincident(g1,g-3)
FEATURE [PartDesign::Pocket] Pocket042
  BaseFeature = -> Pocket041
  Direction = (0,0,-1)
  Length = 2
  Length2 = 100
  Profile = -> Sketch077
  SideType = 0
  Suppressed = false
  Type = 0
  Type2 = 0
FEATURE [Sketcher::SketchObject] Sketch078
  ArcFitTolerance = 0
  AttachmentSupport = -> [Pocket042]
  ExternalGeometry = -> [Pocket042]
  ExternalTypes = [0]
  FullyConstrained = true
  MakeInternals = false
  MapMode = 5
  Placement = pos=(0,0,16) rot=(1,0,0;3.14159rad)
  sketch-geometry (16):
    g0: ArcOfCircle CenterX=-14.5 CenterY=-15.5 CenterZ=0 NormalX=0 NormalY=0 NormalZ=1 AngleXU=0 Radius=1.6 StartAngle=4.71239 EndAngle=7.85398
    g1: ArcOfCircle CenterX=-16.5 CenterY=-15.5 CenterZ=0 NormalX=0 NormalY=0 NormalZ=1 AngleXU=0 Radius=1.6 StartAngle=1.5708 EndAngle=4.71239
    g2: LineSegment StartX=-14.5 StartY=-13.9 StartZ=0 EndX=-16.5 EndY=-13.9 EndZ=0
    g3: LineSegment StartX=-14.5 StartY=-17.1 StartZ=0 EndX=-16.5 EndY=-17.1 EndZ=0
    g4: ArcOfCircle CenterX=-14.5 CenterY=15.5 CenterZ=0 NormalX=0 NormalY=0 NormalZ=1 AngleXU=0 Radius=1.6 StartAngle=4.71239 EndAngle=7.85398
    g5: ArcOfCircle CenterX=-16.5 CenterY=15.5 CenterZ=0 NormalX=0 NormalY=0 NormalZ=1 AngleXU=0 Radius=1.6 StartAngle=1.5708 EndAngle=4.71239
    g6: LineSegment StartX=-14.5 StartY=17.1 StartZ=0 EndX=-16.5 EndY=17.1 EndZ=0
    g7: LineSegment StartX=-14.5 StartY=13.9 StartZ=0 EndX=-16.5 EndY=13.9 EndZ=0
    g8: ArcOfCircle CenterX=16.5 CenterY=15.5 CenterZ=0 NormalX=0 NormalY=0 NormalZ=1 AngleXU=0 Radius=1.6 StartAngle=4.71239 EndAngle=7.85398
    g9: ArcOfCircle CenterX=14.5 CenterY=15.5 CenterZ=0 NormalX=0 NormalY=0 NormalZ=1 AngleXU=0 Radius=1.6 StartAngle=1.5708 EndAngle=4.71239
    g10: LineSegment StartX=16.5 StartY=17.1 StartZ=0 EndX=14.5 EndY=17.1 EndZ=0
    g11: LineSegment StartX=16.5 StartY=13.9 StartZ=0 EndX=14.5 EndY=13.9 EndZ=0
    g12: ArcOfCircle CenterX=16.5 CenterY=-15.5 CenterZ=0 NormalX=0 NormalY=0 NormalZ=1 AngleXU=0 Radius=1.6 StartAngle=4.71239 EndAngle=7.85398
    g13: ArcOfCircle CenterX=14.5 CenterY=-15.5 CenterZ=0 NormalX=0 NormalY=0 NormalZ=1 AngleXU=0 Radius=1.6 StartAngle=1.5708 EndAngle=4.71239
    g14: LineSegment StartX=16.5 StartY=-13.9 StartZ=0 EndX=14.5 EndY=-13.9 EndZ=0
    g15: LineSegment StartX=16.5 StartY=-17.1 StartZ=0 EndX=14.5 EndY=-17.1 EndZ=0
  constraints (36):
    c: Tangent(g0,g3) = 1.5708
    c: Tangent(g0,g2) = -1.5708
    c: Tangent(g2,g1) = -1.5708
    c: Tangent(g3,g1) = 1.5708
    c: Horizontal(g2)
    c: Equal(g0,g1)
    c: Coincident(g0,g-4)
    c: Tangent(g4,g7) = 1.5708
    c: Tangent(g4,g6) = -1.5708
    c: Tangent(g6,g5) = -1.5708
    c: Tangent(g7,g5) = 1.5708
    c: Horizontal(g6)
    c: Equal(g4,g5)
    c: Coincident(g4,g-3)
    c: Tangent(g8,g11) = 1.5708
    c: Tangent(g8,g10) = -1.5708
    c: Tangent(g10,g9) = -1.5708
    c: Tangent(g11,g9) = 1.5708
    c: Horizontal(g10)
    c: Equal(g8,g9)
    c: Coincident(g8,g-6)
    c: Tangent(g12,g15) = 1.5708
    c: Tangent(g12,g14) = -1.5708
    c: Tangent(g14,g13) = -1.5708
    c: Tangent(g15,g13) = 1.5708
    c: Horizontal(g14)
    c: Equal(g12,g13)
    c: Coincident(g12,g-5)
    c: Equal(g0,g-4)
    c: Equal(g-4,g4)
    c: Equal(g4,g8)
    c: Equal(g8,g12)
    c: Equal(g6,g2)
    c: Equal(g2,g14)
    c: Equal(g14,g10)
    c: DistanceX(g14,g14) = 2
FEATURE [PartDesign::Pocket] Pocket043
  BaseFeature = -> Pocket042
  Direction = (0,0,1)
  Length = 5
  Length2 = 100
  Profile = -> Sketch078
  SideType = 0
  Suppressed = false
  Type = 1
  Type2 = 0
FEATURE [Sketcher::SketchObject] Sketch079
  ArcFitTolerance = 0
  AttachmentSupport = -> [Pocket043]
  ExternalGeometry = -> [Pocket043]
  ExternalTypes = [0]
  FullyConstrained = true
  MakeInternals = false
  MapMode = 5
  Placement = pos=(0,0,0) rot=(1,0,0;3.14159rad)
  sketch-geometry (4):
    g0: LineSegment StartX=-19 StartY=21 StartZ=0 EndX=-23 EndY=21 EndZ=0
    g1: LineSegment StartX=-23 StartY=21 StartZ=0 EndX=-23 EndY=-21 EndZ=0
    g2: LineSegment StartX=-23 StartY=-21 StartZ=0 EndX=-19 EndY=-21 EndZ=0
    g3: LineSegment StartX=-19 StartY=-21 StartZ=0 EndX=-19 EndY=21 EndZ=0
  constraints (10):
    c: Coincident(g0,g1)
    c: Coincident(g1,g2)
    c: Coincident(g2,g3)
    c: Coincident(g3,g0)
    c: Horizontal(g0)
    c: Horizontal(g2)
    c: Vertical(g1)
    c: Coincident(g0,g-3)
    c: Coincident(g2,g-3)
    c: DistanceX(g2,g2) = 4
FEATURE [PartDesign::Pocket] Pocket044
  BaseFeature = -> Pocket043
  Direction = (0,0,1)
  Length = 0
  Length2 = 100
  Profile = -> Sketch079
  SideType = 0
  Suppressed = false
  Type = 3
  Type2 = 0
  UpToFace = -> Pocket043 [Face52]
FEATURE [Sketcher::SketchObject] Sketch080
  ArcFitTolerance = 0
  AttachmentSupport = -> [Pocket044]
  ExternalGeometry = -> [Pocket044]
  ExternalTypes = [0]
  FullyConstrained = true
  MakeInternals = false
  MapMode = 5
  Placement = pos=(0,0,20) rot=(0,0,1;0rad)
  sketch-geometry (16):
    g0: ArcOfCircle CenterX=-14.5 CenterY=15.5 CenterZ=0 NormalX=0 NormalY=0 NormalZ=1 AngleXU=0 Radius=3 StartAngle=4.71239 EndAngle=7.85398
    g1: ArcOfCircle CenterX=-16.5 CenterY=15.5 CenterZ=0 NormalX=0 NormalY=0 NormalZ=1 AngleXU=0 Radius=3 StartAngle=1.5708 EndAngle=4.71239
    g2: LineSegment StartX=-14.5 StartY=18.5 StartZ=0 EndX=-16.5 EndY=18.5 EndZ=0
    g3: LineSegment StartX=-14.5 StartY=12.5 StartZ=0 EndX=-16.5 EndY=12.5 EndZ=0
    g4: ArcOfCircle CenterX=16.5 CenterY=15.5 CenterZ=0 NormalX=0 NormalY=0 NormalZ=1 AngleXU=0 Radius=3 StartAngle=4.71239 EndAngle=7.85398
    g5: ArcOfCircle CenterX=14.5 CenterY=15.5 CenterZ=0 NormalX=0 NormalY=0 NormalZ=1 AngleXU=0 Radius=3 StartAngle=1.5708 EndAngle=4.71239
    g6: LineSegment StartX=16.5 StartY=18.5 StartZ=0 EndX=14.5 EndY=18.5 EndZ=0
    g7: LineSegment StartX=16.5 StartY=12.5 StartZ=0 EndX=14.5 EndY=12.5 EndZ=0
    g8: ArcOfCircle CenterX=-14.5 CenterY=-15.5 CenterZ=0 NormalX=0 NormalY=0 NormalZ=1 AngleXU=0 Radius=3 StartAngle=4.71239 EndAngle=7.85398
    g9: ArcOfCircle CenterX=-16.5 CenterY=-15.5 CenterZ=0 NormalX=0 NormalY=0 NormalZ=1 AngleXU=0 Radius=3 StartAngle=1.5708 EndAngle=4.71239
    g10: LineSegment StartX=-14.5 StartY=-12.5 StartZ=0 EndX=-16.5 EndY=-12.5 EndZ=0
    g11: LineSegment StartX=-14.5 StartY=-18.5 StartZ=0 EndX=-16.5 EndY=-18.5 EndZ=0
    g12: ArcOfCircle CenterX=16.5 CenterY=-15.5 CenterZ=0 NormalX=0 NormalY=0 NormalZ=1 AngleXU=0 Radius=3 StartAngle=4.71239 EndAngle=7.85398
    g13: ArcOfCircle CenterX=14.5 CenterY=-15.5 CenterZ=0 NormalX=0 NormalY=0 NormalZ=1 AngleXU=0 Radius=3 StartAngle=1.5708 EndAngle=4.71239
    g14: LineSegment StartX=16.5 StartY=-12.5 StartZ=0 EndX=14.5 EndY=-12.5 EndZ=0
    g15: LineSegment StartX=16.5 StartY=-18.5 StartZ=0 EndX=14.5 EndY=-18.5 EndZ=0
  constraints (36):
    c: Tangent(g0,g3) = 1.5708
    c: Tangent(g0,g2) = -1.5708
    c: Tangent(g2,g1) = -1.5708
    c: Tangent(g3,g1) = 1.5708
    c: Horizontal(g2)
    c: Equal(g0,g1)
    c: Coincident(g0,g-3)
    c: Tangent(g4,g7) = 1.5708
    c: Tangent(g4,g6) = -1.5708
    c: Tangent(g6,g5) = -1.5708
    c: Tangent(g7,g5) = 1.5708
    c: Horizontal(g6)
    c: Equal(g4,g5)
    c: Coincident(g4,g-4)
    c: Tangent(g8,g11) = 1.5708
    c: Tangent(g8,g10) = -1.5708
    c: Tangent(g10,g9) = -1.5708
    c: Tangent(g11,g9) = 1.5708
    c: Horizontal(g10)
    c: Equal(g8,g9)
    c: Coincident(g8,g-6)
    c: Tangent(g12,g15) = 1.5708
    c: Tangent(g12,g14) = -1.5708
    c: Tangent(g14,g13) = -1.5708
    c: Tangent(g15,g13) = 1.5708
    c: Horizontal(g14)
    c: Equal(g12,g13)
    c: Coincident(g12,g-5)
    c: Equal(g12,g0)
    c: Equal(g0,g4)
    c: Equal(g4,g8)
    c: Equal(g8,g-4)
    c: Equal(g10,g14)
    c: Equal(g14,g3)
    c: Equal(g3,g7)
    c: DistanceX(g10,g10) = 2
FEATURE [PartDesign::Pocket] Pocket045
  BaseFeature = -> Pocket044
  Direction = (0,0,-1)
  Length = 0
  Length2 = 100
  Profile = -> Sketch080
  SideType = 0
  Suppressed = false
  Type = 3
  Type2 = 0
  UpToFace = -> Pocket044 [Face89]
FEATURE [Sketcher::SketchObject] Sketch081
  ArcFitTolerance = 0
  AttachmentSupport = -> [Pocket045]
  ExternalGeometry = -> [Pocket045]
  ExternalTypes = [0]
  FullyConstrained = true
  MakeInternals = false
  MapMode = 5
  Placement = pos=(0,0,20) rot=(0,0,1;0rad)
  sketch-geometry (4):
    g0: ArcOfCircle CenterX=0 CenterY=0 CenterZ=0 NormalX=0 NormalY=0 NormalZ=1 AngleXU=0 Radius=11 StartAngle=4.71239 EndAngle=7.85398
    g1: ArcOfCircle CenterX=-2 CenterY=9e-16 CenterZ=0 NormalX=0 NormalY=0 NormalZ=1 AngleXU=0 Radius=11 StartAngle=1.5708 EndAngle=4.71239
    g2: LineSegment StartX=-5.828e-13 StartY=11 StartZ=0 EndX=-2 EndY=11 EndZ=0
    g3: LineSegment StartX=-2e-15 StartY=-11 StartZ=0 EndX=-2 EndY=-11 EndZ=0
  constraints (9):
    c: Tangent(g0,g3) = 1.5708
    c: Tangent(g0,g2) = -1.5708
    c: Tangent(g2,g1) = -1.5708
    c: Tangent(g3,g1) = 1.5708
    c: Horizontal(g2)
    c: Equal(g0,g1)
    c: Coincident(g0,g-1)
    c: Equal(g0,g-3)
    c: DistanceX(g2,g2) = 2
FEATURE [PartDesign::Pocket] Pocket046
  BaseFeature = -> Pocket045
  Direction = (0,0,-1)
  Length = 5
  Length2 = 100
  Profile = -> Sketch081
  SideType = 0
  Suppressed = false
  Type = 1
  Type2 = 0
FEATURE [Sketcher::SketchObject] Sketch082
  ArcFitTolerance = 0
  AttachmentSupport = -> [Pocket046]
  ExternalTypes = [0]
  FullyConstrained = true
  MakeInternals = false
  MapMode = 5
  Placement = pos=(0,0,10) rot=(0,0,1;0rad)
  sketch-geometry (1):
    g0: Circle CenterX=14 CenterY=-65 CenterZ=0 NormalX=0 NormalY=0 NormalZ=1 AngleXU=0 Radius=6.5
  constraints (3):
    c: Diameter(g0) = 13
    c: DistanceX(g0) = 14
    c: DistanceY(g0) = -65
FEATURE [PartDesign::Pocket] Pocket047
  BaseFeature = -> Pocket046
  Direction = (0,0,-1)
  Length = 8
  Length2 = 100
  Profile = -> Sketch082
  SideType = 0
  Suppressed = false
  Type = 0
  Type2 = 0
FEATURE [PartDesign::LinearPattern] LinearPattern004
  Direction = -> Sketch082 [H_Axis]
  Length = 56
  Length2 = 100
  Mode = 0
  Mode2 = 0
  Occurrences = 3
  Occurrences2 = 1
  Offset = 28
  Offset2 = 10
  Reversed = true
  Reversed2 = false
  SpacingPattern = [0]
  SpacingPattern2 = [0]
  Spacings = [-1,-1]
  Suppressed = false
  TransformMode = 0
FEATURE [PartDesign::LinearPattern] LinearPattern005
  Direction = -> Sketch082 [V_Axis]
  Length = 30
  Length2 = 100
  Mode = 0
  Mode2 = 0
  Occurrences = 3
  Occurrences2 = 1
  Offset = 15
  Offset2 = 10
  Reversed2 = false
  SpacingPattern = [0]
  SpacingPattern2 = [0]
  Spacings = [-1,-1]
  Suppressed = false
  TransformMode = 0
FEATURE [PartDesign::MultiTransform] MultiTransform003
  BaseFeature = -> Pocket047
  Originals = -> [Pocket047]
  Refine = true
  Suppressed = false
  TransformMode = 0
  Transformations = -> [LinearPattern004,LinearPattern005]
FEATURE [PartDesign::Body] Body015  label="tube-gearbox-body"
  AllowCompound = true
  Group = -> [Sketch071,Pad028,Sketch072,Pocket037,Sketch073,Pocket038,Sketch074,Pocket039,MultiTransform002,LinearPattern002,LinearPattern003,Sketch075,Pocket040,Chamfer006,Chamfer007,Fillet004,Sketch076,Pocket041,Sketch077,Pocket042,Sketch078,Pocket043,Sketch079,Pocket044,Sketch080,Pocket045,Sketch081,Pocket046,Sketch082,Pocket047,MultiTransform003,LinearPattern004,LinearPattern005]
  Origin = -> Origin024
  Tip = -> MultiTransform003
COMPONENT P18 — recipe-attached ("bearing5201_001", modeled in this document).
Construction recipe (the document's own serialized feature program — sketch geometry with constraints, then the solid features built on it; lengths are millimeters unless a unit is written):

FEATURE [Sketcher::SketchObject] Sketch083
  ArcFitTolerance = 0
  AttachmentSupport = -> [XY_Plane025]
  ExternalTypes = [0]
  FullyConstrained = true
  MakeInternals = false
  MapMode = 5
  sketch-geometry (2):
    g0: Circle CenterX=0 CenterY=0 CenterZ=0 NormalX=0 NormalY=0 NormalZ=1 AngleXU=0 Radius=6
    g1: Circle CenterX=0 CenterY=0 CenterZ=0 NormalX=0 NormalY=0 NormalZ=1 AngleXU=0 Radius=16
  constraints (4):
    c: Coincident(g0,g-1)
    c: Coincident(g1,g0)
    c: Diameter(g0) = 12
    c: Diameter(g1) = 32
FEATURE [PartDesign::Pad] Pad029
  Direction = (0,0,1)
  Length = 15.9
  Length2 = 100
  Profile = -> Sketch083
  SideType = 2
  Suppressed = false
  Type = 0
  Type2 = 0
FEATURE [Sketcher::SketchObject] Sketch084
  ArcFitTolerance = 0
  AttachmentSupport = -> [Pad029]
  ExternalTypes = [0]
  FullyConstrained = true
  MakeInternals = false
  MapMode = 5
  Placement = pos=(0,0,7.95) rot=(0,0,1;0rad)
  sketch-geometry (2):
    g0: Circle CenterX=0 CenterY=0 CenterZ=0 NormalX=0 NormalY=0 NormalZ=1 AngleXU=0 Radius=7.75
    g1: Circle CenterX=0 CenterY=0 CenterZ=0 NormalX=0 NormalY=0 NormalZ=1 AngleXU=0 Radius=13.5
  constraints (4):
    c: Coincident(g0,g-1)
    c: Coincident(g1,g0)
    c: Diameter(g1) = 27
    c: Diameter(g0) = 15.5
FEATURE [PartDesign::Pocket] Pocket048
  BaseFeature = -> Pad029
  Direction = (0,0,-1)
  Length = 1
  Length2 = 100
  Profile = -> Sketch084
  SideType = 0
  Suppressed = false
  Type = 0
  Type2 = 0
FEATURE [PartDesign::Mirrored] Mirrored001
  BaseFeature = -> Pocket048
  MirrorPlane = -> XY_Plane025
  Originals = -> [Pocket048]
  Suppressed = false
  TransformMode = 0
FEATURE [PartDesign::Body] Body016  label="bearing5201"
  AllowCompound = true
  Group = -> [Sketch083,Pad029,Sketch084,Pocket048,Mirrored001]
  Origin = -> Origin025
  Tip = -> Mirrored001
COMPONENT P19 — recipe-attached ("tube-gearbox-output-gear001", modeled in this document).
Construction recipe (the document's own serialized feature program — sketch geometry with constraints, then the solid features built on it; lengths are millimeters unless a unit is written):

FEATURE [Sketcher::SketchObject] Sketch085
  ArcFitTolerance = 0
  AttachmentSupport = -> [YZ_Plane026]
  ExternalTypes = [0]
  FullyConstrained = true
  MakeInternals = false
  MapMode = 5
  Placement = pos=(0,0,0) rot=(0.57735,0.57735,0.57735;2.0944rad)
  sketch-geometry (6):
    g0: LineSegment StartX=0 StartY=20 StartZ=0 EndX=7 EndY=20 EndZ=0
    g1: LineSegment StartX=7 StartY=20 StartZ=0 EndX=7 EndY=5 EndZ=0
    g2: LineSegment StartX=7 StartY=5 StartZ=0 EndX=3.9 EndY=5 EndZ=0
    g3: LineSegment StartX=3.9 StartY=5 StartZ=0 EndX=3.9 EndY=-20 EndZ=0
    g4: LineSegment StartX=3.9 StartY=-20 StartZ=0 EndX=0 EndY=-20 EndZ=0
    g5: LineSegment StartX=0 StartY=-20 StartZ=0 EndX=0 EndY=20 EndZ=0
  constraints (18):
    c: PointOnObject(g0,g-2)
    c: Horizontal(g0)
    c: Coincident(g0,g1)
    c: Vertical(g1)
    c: Coincident(g1,g2)
    c: Horizontal(g2)
    c: Coincident(g2,g3)
    c: Vertical(g3)
    c: Coincident(g3,g4)
    c: PointOnObject(g4,g-2)
    c: Horizontal(g4)
    c: Coincident(g4,g5)
    c: Coincident(g5,g0)
    c: DistanceX(g0) = 7
    c: DistanceY(g0) = 20
    c: DistanceX(g2) = 3.9
    c: DistanceY(g4) = -20
    c: DistanceY(g1) = 5
FEATURE [Sketcher::SketchObject] Sketch086
  ArcFitTolerance = 0
  AttachmentSupport = -> [XZ_Plane026]
  ExternalTypes = [0]
  FullyConstrained = true
  MakeInternals = false
  MapMode = 5
  Placement = pos=(0,0,0) rot=(1,0,0;1.5708rad)
  sketch-geometry (4):
    g0: LineSegment StartX=-28 StartY=0 StartZ=0 EndX=-25.8162 EndY=-6 EndZ=0
    g1: LineSegment StartX=-25.8162 StartY=-6 StartZ=0 EndX=-14.1838 EndY=-6 EndZ=0
    g2: LineSegment StartX=-14.1838 StartY=-6 StartZ=0 EndX=-12 EndY=0 EndZ=0
    g3: LineSegment StartX=-12 StartY=0 StartZ=0 EndX=-28 EndY=0 EndZ=0
  constraints (12):
    c: Coincident(g0,g1)
    c: Horizontal(g1)
    c: Coincident(g1,g2)
    c: Coincident(g2,g3)
    c: Coincident(g3,g0)
    c: Horizontal(g3)
    c: DistanceY(g1) = -6
    c: DistanceX(g0) = -28
    c: DistanceX(g2) = -12
    c: DistanceY(g2) = 0
    c: Equal(g2,g0)
    c: Angle(g2,g1) = 1.91986
FEATURE [Sketcher::SketchObject] Sketch087
  ArcFitTolerance = 0
  AttachmentSupport = -> [XY_Plane026]
  ExternalTypes = [0]
  FullyConstrained = true
  MakeInternals = false
  MapMode = 5
  sketch-geometry (1):
    g0: Circle CenterX=0 CenterY=20 CenterZ=0 NormalX=0 NormalY=0 NormalZ=1 AngleXU=0 Radius=5
  constraints (3):
    c: PointOnObject(g0,g-2)
    c: Diameter(g0) = 10
    c: DistanceY(g0) = 20
FEATURE [PartDesign::FeatureBase] BaseFeature003
  BaseFeature = -> Fusion
  Suppressed = false
FEATURE [PartDesign::Groove] Groove002
  Angle = 360
  Angle2 = 60
  Axis = (0,0,1)
  Base = (0,0,0)
  BaseFeature = -> BaseFeature003
  Profile = -> Sketch085
  ReferenceAxis = -> Sketch085 [V_Axis]
  Suppressed = false
  Type = 0
FEATURE [PartDesign::Groove] Groove003
  Angle = 360
  Angle2 = 60
  Axis = (0,2e-16,1)
  Base = (0,0,0)
  BaseFeature = -> Groove002
  Profile = -> Sketch086
  ReferenceAxis = -> Sketch086 [V_Axis]
  Reversed = true
  Suppressed = false
  Type = 0
FEATURE [PartDesign::Pocket] Pocket049
  BaseFeature = -> Groove003
  Direction = (0,0,-1)
  Length = 5
  Length2 = 100
  Profile = -> Sketch087
  SideType = 0
  Suppressed = false
  Type = 1
  Type2 = 0
FEATURE [PartDesign::PolarPattern] PolarPattern007
  Angle = 360
  Axis = -> Sketch087 [N_Axis]
  BaseFeature = -> Pocket049
  Mode = 0
  Occurrences = 8
  Offset = 120
  Originals = -> [Pocket049]
  SpacingPattern = [0]
  Spacings = [-1,-1,-1,-1,-1,-1,-1]
  Suppressed = false
  TransformMode = 0
FEATURE [PartDesign::Body] Body017  label="gearbox-output-gear"
  AllowCompound = true
  BaseFeature = -> Fusion
  Group = -> [BaseFeature003,Sketch085,Groove002,Sketch086,Groove003,Sketch087,Pocket049,PolarPattern007]
  Origin = -> Origin026
  Placement = pos=(0,0,0) rot=(0,0,1;0.15708rad)
  Tip = -> PolarPattern007
COMPONENT P20 — recipe-attached ("m8-bolt-sleeve001", modeled in this document).
Construction recipe (the document's own serialized feature program — sketch geometry with constraints, then the solid features built on it; lengths are millimeters unless a unit is written):

FEATURE [Sketcher::SketchObject] Sketch088
  ArcFitTolerance = 0
  AttachmentSupport = -> [XY_Plane028]
  ExternalTypes = [0]
  FullyConstrained = true
  MakeInternals = false
  MapMode = 5
  sketch-geometry (1):
    g0: Circle CenterX=0 CenterY=0 CenterZ=0 NormalX=0 NormalY=0 NormalZ=1 AngleXU=0 Radius=7
  constraints (2):
    c: Coincident(g0,g-1)
    c: Diameter(g0) = 14
FEATURE [PartDesign::Pad] Pad030
  Direction = (0,0,1)
  Length = 1
  Length2 = 100
  Profile = -> Sketch088
  SideType = 0
  Suppressed = false
  Type = 0
  Type2 = 0
FEATURE [Sketcher::SketchObject] Sketch089
  ArcFitTolerance = 0
  AttachmentSupport = -> [Pad030]
  ExternalTypes = [0]
  FullyConstrained = true
  MakeInternals = false
  MapMode = 5
  Placement = pos=(0,0,1) rot=(0,0,1;0rad)
  sketch-geometry (1):
    g0: Circle CenterX=0 CenterY=0 CenterZ=0 NormalX=0 NormalY=0 NormalZ=1 AngleXU=0 Radius=6
  constraints (2):
    c: Coincident(g0,g-1)
    c: Diameter(g0) = 12
FEATURE [PartDesign::Pad] Pad031
  BaseFeature = -> Pad030
  Direction = (0,0,1)
  Length = 15.5
  Length2 = 100
  Profile = -> Sketch089
  SideType = 0
  Suppressed = false
  Type = 0
  Type2 = 0
FEATURE [PartDesign::Chamfer] Chamfer008
  Angle = 45
  Base = -> Pad031 [Edge6]
  BaseFeature = -> Pad031
  ChamferType = 0
  FlipDirection = false
  Size = 1
  Size2 = 1
  SupportTransform = true
  Suppressed = false
  UseAllEdges = false
FEATURE [Sketcher::SketchObject] Sketch090
  ArcFitTolerance = 0
  AttachmentSupport = -> [Chamfer008]
  ExternalTypes = [0]
  FullyConstrained = true
  MakeInternals = false
  MapMode = 5
  Placement = pos=(0,0,16.5) rot=(0,0,1;0rad)
  sketch-geometry (1):
    g0: Circle CenterX=0 CenterY=0 CenterZ=0 NormalX=0 NormalY=0 NormalZ=1 AngleXU=0 Radius=3.85
  constraints (3):
    c: PointOnObject(g0,g-2)
    c: Diameter(g0) = 7.7
    c: DistanceY(g0) = 0
FEATURE [PartDesign::Pocket] Pocket050
  BaseFeature = -> Chamfer008
  Direction = (0,0,-1)
  Length = 5
  Length2 = 100
  Profile = -> Sketch090
  SideType = 0
  Suppressed = false
  Type = 1
  Type2 = 0
FEATURE [PartDesign::Body] Body018  label="m8-bolt-sleeve"
  AllowCompound = true
  Group = -> [Sketch088,Pad030,Sketch089,Pad031,Chamfer008,Sketch090,Pocket050]
  Origin = -> Origin028
  Tip = -> Pocket050
COMPONENT P21 — recipe-attached ("bolt-m8x40imb001", modeled in this document).
Construction recipe (the document's own serialized feature program — sketch geometry with constraints, then the solid features built on it; lengths are millimeters unless a unit is written):

FEATURE [PartDesign::FeatureBase] BaseFeature004
  BaseFeature = -> BOLTS_part
  Suppressed = false
FEATURE [PartDesign::Body] Body019  label="m8x40imb"
  AllowCompound = true
  BaseFeature = -> BOLTS_part
  Group = -> [BaseFeature004]
  Origin = -> Origin029
  Tip = -> BaseFeature004
COMPONENT P22 — same part as P10; its construction recipe is shown at P10.
COMPONENT P23 — recipe-attached ("tube-gearbox-motor-gear001", modeled in this document).
Construction recipe (the document's own serialized feature program — sketch geometry with constraints, then the solid features built on it; lengths are millimeters unless a unit is written):

FEATURE [PartDesign::FeatureBase] BaseFeature005
  BaseFeature = -> InvoluteGear001
  Suppressed = false
FEATURE [Sketcher::SketchObject] Sketch091
  ArcFitTolerance = 0
  AttachmentSupport = -> [BaseFeature005]
  ExternalTypes = [0]
  FullyConstrained = true
  MakeInternals = false
  MapMode = 5
  Placement = pos=(0,0,0) rot=(1,0,0;3.14159rad)
  sketch-geometry (2):
    g0: ArcOfCircle CenterX=0 CenterY=0 CenterZ=0 NormalX=0 NormalY=0 NormalZ=1 AngleXU=0 Radius=2.55 StartAngle=0.636936 EndAngle=5.64625
    g1: LineSegment StartX=2.05 StartY=1.51658 StartZ=0 EndX=2.05 EndY=-1.51658 EndZ=0
  constraints (6):
    c: Coincident(g0,g-1)
    c: Diameter(g0) = 5.1
    c: Vertical(g1)
    c: Coincident(g0,g1)
    c: Coincident(g0,g1)
    c: DistanceX(g0) = 2.05
FEATURE [PartDesign::Pocket] Pocket051
  BaseFeature = -> BaseFeature005
  Direction = (0,0,1)
  Length = 25
  Length2 = 100
  Profile = -> Sketch091
  SideType = 0
  Suppressed = false
  Type = 1
  Type2 = 0
FEATURE [PartDesign::Chamfer] Chamfer009
  Angle = 45
  Base = -> Pocket051 [Edge199,Edge200]
  BaseFeature = -> Pocket051
  ChamferType = 1
  FlipDirection = false
  Size = 0.5
  Size2 = 1
  SupportTransform = true
  Suppressed = false
  UseAllEdges = false
FEATURE [PartDesign::Body] Body020  label="tube-motor-gear"
  AllowCompound = true
  BaseFeature = -> InvoluteGear001
  Group = -> [BaseFeature005,Sketch091,Pocket051,Chamfer009]
  Origin = -> Origin031
  Placement = pos=(0,0,0) rot=(0,0,1;0.139626rad)
  Tip = -> Chamfer009
COMPONENT P24 — recipe-attached ("bearing_51126_cover001", modeled in this document).
Construction recipe (the document's own serialized feature program — sketch geometry with constraints, then the solid features built on it; lengths are millimeters unless a unit is written):

FEATURE [Sketcher::SketchObject] Sketch019
  ArcFitTolerance = 0
  AttachmentSupport = -> [XZ_Plane011]
  ExternalTypes = [0]
  FullyConstrained = true
  MakeInternals = false
  MapMode = 5
  Placement = pos=(0,0,0) rot=(1,0,0;1.5708rad)
  sketch-geometry (5):
    g0: LineSegment StartX=85 StartY=0 StartZ=0 EndX=85 EndY=28.5 EndZ=0
    g1: LineSegment StartX=85 StartY=28.5 StartZ=0 EndX=84.5 EndY=29 EndZ=0
    g2: LineSegment StartX=84.5 StartY=29 StartZ=0 EndX=87 EndY=29 EndZ=0
    g3: LineSegment StartX=87 StartY=29 StartZ=0 EndX=87 EndY=0 EndZ=0
    g4: LineSegment StartX=87 StartY=0 StartZ=0 EndX=85 EndY=0 EndZ=0
  constraints (15):
    c: PointOnObject(g0,g-1)
    c: Vertical(g0)
    c: Coincident(g0,g1)
    c: Coincident(g1,g2)
    c: Coincident(g2,g3)
    c: PointOnObject(g3,g-1)
    c: Vertical(g3)
    c: Coincident(g3,g4)
    c: Coincident(g4,g0)
    c: Horizontal(g2)
    c: Angle(g1,g2) = 0.785398
    c: DistanceX(g0) = 85
    c: DistanceX(g4,g4) = 2
    c: DistanceX(g2,g2) = 2.5
    c: DistanceY(g3,g3) = 29
FEATURE [PartDesign::Revolution] Revolution
  Angle = 360
  Angle2 = 60
  Axis = (0,2e-16,1)
  Base = (0,0,0)
  Placement = pos=(0,0,0) rot=(1,0,0;1.5708rad)
  Profile = -> Sketch019
  ReferenceAxis = -> Sketch019 [V_Axis]
  Reversed = true
  Suppressed = false
  Type = 0
FEATURE [Sketcher::SketchObject] Sketch020
  ArcFitTolerance = 0
  AttachmentSupport = -> [Revolution]
  ExternalTypes = [0]
  FullyConstrained = true
  MakeInternals = false
  MapMode = 5
  Placement = pos=(0,0,0) rot=(1,0,0;3.14159rad)
  sketch-geometry (1):
    g0: Circle CenterX=0 CenterY=0 CenterZ=0 NormalX=0 NormalY=0 NormalZ=1 AngleXU=0 Radius=86
  constraints (2):
    c: Coincident(g0,g-1)
    c: Diameter(g0) = 172
FEATURE [PartDesign::Pocket] Pocket013
  BaseFeature = -> Revolution
  Direction = (0,0,1)
  Length = 25
  Length2 = 100
  Placement = pos=(0,0,0) rot=(1,0,0;1.5708rad)
  Profile = -> Sketch020
  SideType = 0
  Suppressed = false
  Type = 0
  Type2 = 0
FEATURE [PartDesign::Chamfer] Chamfer003
  Angle = 45
  Base = -> Pocket013 [Edge1,Edge8]
  BaseFeature = -> Pocket013
  ChamferType = 0
  FlipDirection = false
  Placement = pos=(0,0,0) rot=(1,0,0;1.5708rad)
  Size = 0.5
  Size2 = 1
  SupportTransform = true
  Suppressed = false
  UseAllEdges = false
FEATURE [PartDesign::Body] Body006  label="bearing-51126-cover"
  AllowCompound = true
  Group = -> [Sketch019,Revolution,Sketch020,Pocket013,Chamfer003]
  Origin = -> Origin011
  Tip = -> Chamfer003
COMPONENT P25 — recipe-attached ("bearing-top-location-ring001", modeled in this document).
Construction recipe (the document's own serialized feature program — sketch geometry with constraints, then the solid features built on it; lengths are millimeters unless a unit is written):

FEATURE [Sketcher::SketchObject] Sketch015
  ArcFitTolerance = 0
  AttachmentSupport = -> [XY_Plane010]
  ExternalTypes = [0]
  FullyConstrained = true
  MakeInternals = false
  MapMode = 5
  sketch-geometry (7):
    g0: ArcOfCircle CenterX=0 CenterY=0 CenterZ=0 NormalX=0 NormalY=0 NormalZ=1 AngleXU=0 Radius=60 StartAngle=1.65423 EndAngle=3.58176
    g1: ArcOfCircle CenterX=0 CenterY=0 CenterZ=0 NormalX=0 NormalY=0 NormalZ=1 AngleXU=0 Radius=10 StartAngle=2.0944 EndAngle=3.14159
    g2: LineSegment StartX=-5 StartY=8.66025 StartZ=0 EndX=-5 EndY=59.7913 EndZ=0
    g3: LineSegment [constr] StartX=0 StartY=0 StartZ=0 EndX=-86.6025 EndY=-50 EndZ=0
    g4: LineSegment StartX=-10 StartY=1.2e-15 StartZ=0 EndX=-54.2808 EndY=-25.5655 EndZ=0
    g5: LineSegment [constr] StartX=-10 StartY=1.2e-15 StartZ=0 EndX=0 EndY=0 EndZ=0
    g6: Circle CenterX=0 CenterY=50 CenterZ=0 NormalX=0 NormalY=0 NormalZ=1 AngleXU=0 Radius=2
  constraints (20):
    c: Coincident(g0,g-1)
    c: Coincident(g1,g0)
    c: Vertical(g2)
    c: Coincident(g3,g0)
    c: Angle(g3) = -2.61799
    c: Parallel(g4,g3)
    c: Diameter(g0) = 120
    c: Coincident(g5,g4)
    c: Coincident(g5,g0)
    c: Coincident(g0,g2)
    c: Coincident(g0,g4)
    c: Coincident(g1,g2)
    c: DistanceX(g1) = -5
    c: Diameter(g1) = 20
    c: Distance(g1,g3) = 5
    c: Coincident(g4,g1)
    c: Distance(g3) = 100
    c: PointOnObject(g6,g-2)
    c: Diameter(g6) = 4
    c: DistanceY(g6) = 50
FEATURE [Sketcher::SketchObject] Sketch016
  ArcFitTolerance = 0
  AttachmentSupport = -> [XY_Plane010]
  ExternalTypes = [0]
  FullyConstrained = true
  MakeInternals = false
  MapMode = 5
  sketch-geometry (1):
    g0: Circle CenterX=0 CenterY=0 CenterZ=0 NormalX=0 NormalY=0 NormalZ=1 AngleXU=0 Radius=5.5
  constraints (2):
    c: Coincident(g0,g-1)
    c: Diameter(g0) = 11
FEATURE [Sketcher::SketchObject] Sketch017
  ArcFitTolerance = 0
  AttachmentSupport = -> [XY_Plane010]
  ExternalTypes = [0]
  FullyConstrained = true
  MakeInternals = false
  MapMode = 5
  sketch-geometry (1):
    g0: Circle CenterX=0 CenterY=0 CenterZ=0 NormalX=0 NormalY=0 NormalZ=1 AngleXU=0 Radius=66.25
  constraints (2):
    c: Coincident(g0,g-1)
    c: Diameter(g0) = 132.5
FEATURE [PartDesign::Pad] Pad004
  Direction = (0,0,1)
  Length = 6
  Length2 = 100
  Profile = -> Sketch017
  SideType = 0
  Suppressed = false
  Type = 0
  Type2 = 0
FEATURE [PartDesign::Pocket] Pocket010
  BaseFeature = -> Pad004
  Direction = (0,0,-1)
  Length = 5
  Length2 = 100
  Profile = -> Sketch016
  Reversed = true
  SideType = 0
  Suppressed = false
  Type = 1
  Type2 = 0
FEATURE [PartDesign::Pocket] Pocket011
  BaseFeature = -> Pocket010
  Direction = (0,0,-1)
  Length = 5
  Length2 = 100
  Profile = -> Sketch015
  Reversed = true
  SideType = 0
  Suppressed = false
  Type = 1
  Type2 = 0
FEATURE [PartDesign::PolarPattern] PolarPattern003
  Angle = 360
  Axis = -> Sketch015 [N_Axis]
  BaseFeature = -> Pocket011
  Mode = 0
  Occurrences = 3
  Offset = 120
  Originals = -> [Pocket011]
  SpacingPattern = [0]
  Spacings = [-1,-1]
  Suppressed = false
  TransformMode = 0
FEATURE [PartDesign::Chamfer] Chamfer002
  Angle = 45
  Base = -> PolarPattern003 [Edge3,Edge2]
  BaseFeature = -> PolarPattern003
  ChamferType = 0
  FlipDirection = false
  Size = 1
  Size2 = 1
  SupportTransform = true
  Suppressed = false
  UseAllEdges = false
FEATURE [PartDesign::Fillet] Fillet001
  Base = -> Chamfer002 [Edge49,Edge46,Edge54,Edge52,Edge42,Edge40]
  BaseFeature = -> Chamfer002
  Radius = 6
  SupportTransform = true
  Suppressed = false
  UseAllEdges = false
FEATURE [Sketcher::SketchObject] Sketch018
  ArcFitTolerance = 0
  AttachmentSupport = -> [Fillet001]
  ExternalTypes = [0]
  FullyConstrained = true
  MakeInternals = false
  MapMode = 5
  Placement = pos=(0,0,6) rot=(0,0,1;0rad)
  sketch-geometry (1):
    g0: Circle CenterX=0 CenterY=0 CenterZ=0 NormalX=0 NormalY=0 NormalZ=1 AngleXU=0 Radius=64
  constraints (2):
    c: Coincident(g0,g-1)
    c: Diameter(g0) = 128
FEATURE [PartDesign::Pocket] Pocket012
  BaseFeature = -> Fillet001
  Direction = (0,0,-1)
  Length = 3
  Length2 = 100
  Profile = -> Sketch018
  SideType = 0
  Suppressed = false
  Type = 0
  Type2 = 0
FEATURE [PartDesign::Body] Body005  label="bearing-top-location-ring"
  AllowCompound = true
  Group = -> [Sketch017,Pad004,Sketch016,Pocket010,Sketch015,Pocket011,PolarPattern003,Chamfer002,Fillet001,Sketch018,Pocket012]
  Origin = -> Origin010
  Placement = pos=(0,0,48) rot=(0.999999,-0.001422,0;3.14159rad)
  Tip = -> Pocket012
COMPONENT P26 — geometry summary ("bearing-51127"; no construction recipe available for this part):
  bounding box: 22.4 x 22.0 x 8.4 mm
  tessellated surface: 20,826 triangles
  volume: 1529 mm^3 (37% of its bounding box)
COMPONENT P27 — geometry summary ("bearing-51128"; no construction recipe available for this part):
  bounding box: 22.4 x 22.0 x 8.4 mm
  tessellated surface: 20,826 triangles
  volume: 1529 mm^3 (37% of its bounding box)
COMPONENT P28 — geometry summary ("bearing-51129"; no construction recipe available for this part):
  bounding box: 22.4 x 22.0 x 8.4 mm
  tessellated surface: 20,826 triangles
  volume: 1529 mm^3 (37% of its bounding box)
COMPONENT P29 — geometry summary ("bearing-51130"; no construction recipe available for this part):
  bounding box: 22.4 x 22.0 x 8.4 mm
  tessellated surface: 20,826 triangles
  volume: 1529 mm^3 (37% of its bounding box)
COMPONENT P30 — recipe-attached ("eccentric-sleeve001", modeled in this document).
Construction recipe (the document's own serialized feature program — sketch geometry with constraints, then the solid features built on it; lengths are millimeters unless a unit is written):

FEATURE [Sketcher::SketchObject] Sketch092
  ArcFitTolerance = 0
  AttachmentSupport = -> [XY_Plane033]
  ExternalTypes = [0]
  FullyConstrained = true
  MakeInternals = false
  MapMode = 5
  sketch-geometry (1):
    g0: Circle CenterX=0 CenterY=0 CenterZ=0 NormalX=0 NormalY=0 NormalZ=1 AngleXU=0 Radius=8
  constraints (2):
    c: Coincident(g0,g-1)
    c: Diameter(g0) = 16
FEATURE [PartDesign::Pad] Pad032
  Direction = (0,0,1)
  Length = 4
  Length2 = 100
  Profile = -> Sketch092
  SideType = 0
  Suppressed = false
  Type = 0
  Type2 = 0
FEATURE [Sketcher::SketchObject] Sketch093
  ArcFitTolerance = 0
  AttachmentSupport = -> [Pad032]
  ExternalTypes = [0]
  FullyConstrained = true
  MakeInternals = false
  MapMode = 5
  Placement = pos=(0,0,4) rot=(0,0,1;0rad)
  sketch-geometry (1):
    g0: Circle CenterX=0 CenterY=0 CenterZ=0 NormalX=0 NormalY=0 NormalZ=1 AngleXU=0 Radius=4
  constraints (2):
    c: Coincident(g0,g-1)
    c: Diameter(g0) = 8
FEATURE [PartDesign::Pad] Pad033
  BaseFeature = -> Pad032
  Direction = (0,0,1)
  Length = 7
  Length2 = 100
  Profile = -> Sketch093
  SideType = 0
  Suppressed = false
  Type = 0
  Type2 = 0
FEATURE [Sketcher::SketchObject] Sketch094
  ArcFitTolerance = 0
  AttachmentSupport = -> [Pad033]
  ExternalTypes = [0]
  FullyConstrained = true
  MakeInternals = false
  MapMode = 5
  Placement = pos=(0,0,11) rot=(0,0,1;0rad)
  sketch-geometry (4):
    g0: ArcOfCircle CenterX=0 CenterY=0 CenterZ=0 NormalX=0 NormalY=0 NormalZ=1 AngleXU=0 Radius=4.05 StartAngle=5.44901 EndAngle=7.11736
    g1: LineSegment StartX=1 StartY=3 StartZ=0 EndX=2.72075 EndY=3 EndZ=0
    g2: LineSegment StartX=1 StartY=-3 StartZ=0 EndX=2.72075 EndY=-3 EndZ=0
    g3: ArcOfCircle CenterX=1 CenterY=0 CenterZ=0 NormalX=0 NormalY=0 NormalZ=1 AngleXU=0 Radius=3 StartAngle=1.5708 EndAngle=4.71239
  constraints (11):
    c: Coincident(g0,g-1)
    c: Diameter(g0) = 8.1
    c: Horizontal(g2)
    c: Horizontal(g1)
    c: Coincident(g0,g2)
    c: Coincident(g0,g1)
    c: PointOnObject(g3,g-1)
    c: DistanceX(g3) = 1
    c: Tangent(g3,g1) = 1.5708
    c: Tangent(g3,g2) = -1.5708
    c: Diameter(g3) = 6
FEATURE [PartDesign::Pocket] Pocket052
  BaseFeature = -> Pad033
  Direction = (0,0,-1)
  Length = 5
  Length2 = 100
  Profile = -> Sketch094
  SideType = 0
  Suppressed = false
  Type = 1
  Type2 = 0
FEATURE [PartDesign::Fillet] Fillet005
  Base = -> Pocket052 [Edge15,Edge20]
  BaseFeature = -> Pocket052
  Radius = 0.3
  SupportTransform = true
  Suppressed = false
  UseAllEdges = false
FEATURE [PartDesign::Fillet] Fillet006
  Base = -> Fillet005 [Edge20,Edge24]
  BaseFeature = -> Fillet005
  Radius = 2
  SupportTransform = true
  Suppressed = false
  UseAllEdges = false
FEATURE [PartDesign::Chamfer] Chamfer010
  Angle = 5
  Base = -> Fillet006 [Edge9]
  BaseFeature = -> Fillet006
  ChamferType = 2
  FlipDirection = false
  Size = 3
  Size2 = 1
  SupportTransform = true
  Suppressed = false
  UseAllEdges = false
FEATURE [PartDesign::Chamfer] Chamfer011
  Angle = 45
  Base = -> Chamfer010 [Edge34,Edge14,Edge18,Edge22,Edge26,Edge29]
  BaseFeature = -> Chamfer010
  ChamferType = 1
  FlipDirection = false
  Size = 0.5
  Size2 = 1
  SupportTransform = true
  Suppressed = false
  UseAllEdges = false
FEATURE [PartDesign::Body] Body021  label="eccentric-sleeve"
  AllowCompound = true
  Group = -> [Sketch092,Pad032,Sketch093,Pad033,Sketch094,Pocket052,Fillet005,Fillet006,Chamfer010,Chamfer011]
  Origin = -> Origin064
  Tip = -> Chamfer011
COMPONENT P31 — same part as P30; its construction recipe is shown at P30.
COMPONENT P32 — same part as P30; its construction recipe is shown at P30.
COMPONENT P33 — same part as P30; its construction recipe is shown at P30.
PROVENANCE & LICENSES
A FreeCAD (.FCStd) document from a public repository crawl; recipes are the document's own serialized feature recipes (and, for linked parts, companion documents' recipes).
License: bsd.
